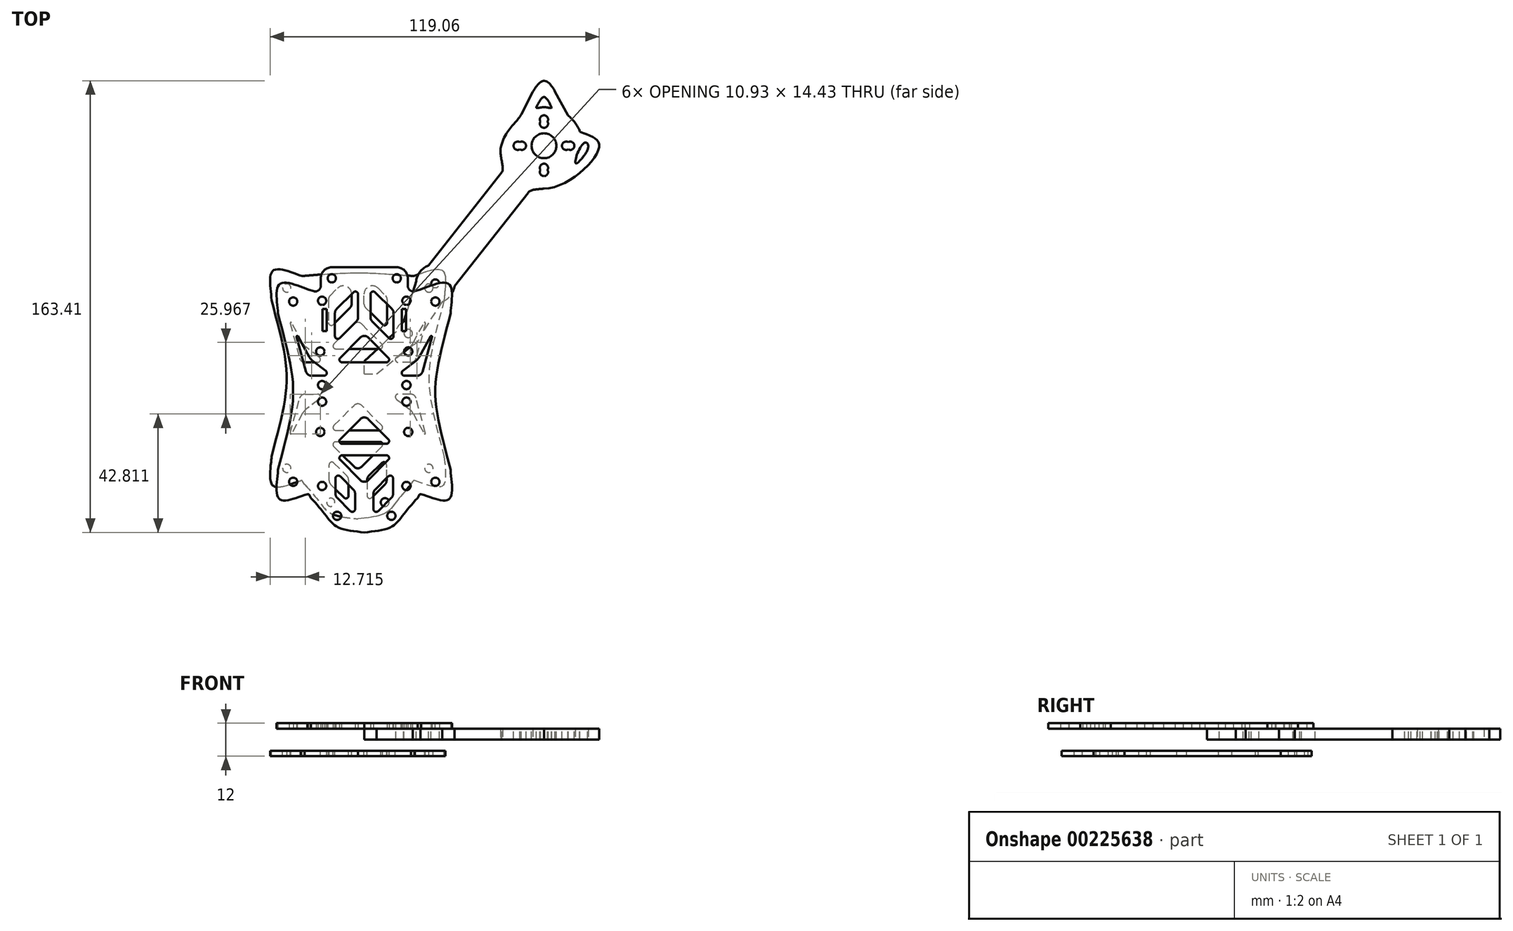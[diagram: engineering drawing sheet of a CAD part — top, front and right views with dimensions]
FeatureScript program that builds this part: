
annotation { "Feature Type Name" : "Feature", "Feature Type Description" : "" }
export const myFeature = defineFeature(function(context is Context, id is Id, definition is map)
    precondition{}
    {
        {
            var Q0;
            Q0=qCreatedBy(makeId("Top.planeOp"),FACE);
            var sketch = newSketch(context, id + "F0", { "sketchPlane" : qUnion([Q0])});
            skPoint(sketch, "E0.middle", {"position": v(0, -4.73) * mm});
            skLineSegment(sketch, "E1.bottom", {"start": v(25.7, 27.89) * mm, "end": v(-25.7, 27.89) * mm, "construction": true});
            skLineSegment(sketch, "E1.top", {"start": v(25.7, -37.35) * mm, "end": v(-25.7, -37.35) * mm, "construction": true});
            skLineSegment(sketch, "E1.left", {"start": v(25.7, 27.89) * mm, "end": v(25.7, -37.35) * mm, "construction": true});
            skLineSegment(sketch, "E1.right", {"start": v(-25.7, 27.89) * mm, "end": v(-25.7, -37.35) * mm, "construction": true});
            skLineSegment(sketch, "E2.bottom", {"start": v(-65, 77.77) * mm, "end": v(65, 77.77) * mm, "construction": true});
            skLineSegment(sketch, "E2.top", {"start": v(-65, -87.23) * mm, "end": v(65, -87.23) * mm, "construction": true});
            skLineSegment(sketch, "E2.left", {"start": v(-65, 77.77) * mm, "end": v(-65, -87.23) * mm, "construction": true});
            skLineSegment(sketch, "E2.right", {"start": v(65, 77.77) * mm, "end": v(65, -87.23) * mm, "construction": true});
            skCircle(sketch, "E3", {"center": v(65, 77.77) * mm, "radius": 4.5 * mm, "construction": true});
            skCircle(sketch, "E4", {"center": v(-65, 77.77) * mm, "radius": 4.5 * mm, "construction": true});
            skCircle(sketch, "E5", {"center": v(65, -87.23) * mm, "radius": 4.5 * mm, "construction": true});
            skCircle(sketch, "E6", {"center": v(-65, -87.23) * mm, "radius": 4.5 * mm, "construction": true});
            skCircle(sketch, "E7", {"center": v(65, 77.77) * mm, "radius": 8 * mm, "construction": true});
            skCircle(sketch, "E8", {"center": v(65, -87.23) * mm, "radius": 8 * mm, "construction": true});
            skCircle(sketch, "E9", {"center": v(-65, -87.23) * mm, "radius": 8 * mm, "construction": true});
            skCircle(sketch, "E10", {"center": v(-65, 77.77) * mm, "radius": 8 * mm, "construction": true});
            skCircle(sketch, "E11", {"center": v(65, 77.77) * mm, "radius": 9.5 * mm, "construction": true});
            skCircle(sketch, "E12", {"center": v(65, -87.23) * mm, "radius": 9.5 * mm, "construction": true});
            skCircle(sketch, "E13", {"center": v(-65, -87.23) * mm, "radius": 9.5 * mm, "construction": true});
            skCircle(sketch, "E14", {"center": v(-65, 77.77) * mm, "radius": 9.5 * mm, "construction": true});
            skCircle(sketch, "E15", {"center": v(65, 77.77) * mm, "radius": 14 * mm, "construction": true});
            skCircle(sketch, "E16", {"center": v(-65, 77.77) * mm, "radius": 14 * mm, "construction": true});
            skCircle(sketch, "E17", {"center": v(65, -87.23) * mm, "radius": 14 * mm, "construction": true});
            skCircle(sketch, "E18", {"center": v(-65, -87.23) * mm, "radius": 14 * mm, "construction": true});
            skCircle(sketch, "E19", {"center": v(65, 77.77) * mm, "radius": 63.5 * mm, "construction": true});
            skCircle(sketch, "E20", {"center": v(65, -87.23) * mm, "radius": 63.5 * mm, "construction": true});
            skCircle(sketch, "E21", {"center": v(-65, -87.23) * mm, "radius": 63.5 * mm, "construction": true});
            skCircle(sketch, "E22", {"center": v(-65, 77.77) * mm, "radius": 63.5 * mm, "construction": true});
            skLineSegment(sketch, "E23.bottom", {"start": v(-26.2, 21.46) * mm, "end": v(26.2, 21.46) * mm, "construction": true});
            skLineSegment(sketch, "E23.top", {"start": v(-26.19, -30.92) * mm, "end": v(26.2, -30.92) * mm, "construction": true});
            skLineSegment(sketch, "E23.left", {"start": v(-26.2, 21.46) * mm, "end": v(-26.2, -30.92) * mm, "construction": true});
            skLineSegment(sketch, "E23.right", {"start": v(26.2, 21.46) * mm, "end": v(26.2, -30.92) * mm, "construction": true});
            skCircle(sketch, "E24", {"center": v(25.7, 27.89) * mm, "radius": 1.5 * mm, "construction": true});
            skCircle(sketch, "E25", {"center": v(-25.7, 27.89) * mm, "radius": 1.5 * mm, "construction": true});
            skCircle(sketch, "E26", {"center": v(25.7, -37.35) * mm, "radius": 1.5 * mm, "construction": true});
            skCircle(sketch, "E27", {"center": v(-25.7, -37.35) * mm, "radius": 1.5 * mm, "construction": true});
            skLineSegment(sketch, "E28", {"start": v(-65, 77.77) * mm, "end": v(65, -87.23) * mm, "construction": true});
            skLineSegment(sketch, "E29", {"start": v(65, 77.77) * mm, "end": v(-65, -87.23) * mm, "construction": true});
            skLineSegment(sketch, "E30.bottom", {"start": v(-15.25, -8.35) * mm, "end": v(15.25, -8.35) * mm, "construction": true});
            skLineSegment(sketch, "E30.top", {"start": v(-15.25, -38.85) * mm, "end": v(15.25, -38.85) * mm, "construction": true});
            skLineSegment(sketch, "E30.left", {"start": v(-15.25, -8.35) * mm, "end": v(-15.25, -38.85) * mm, "construction": true});
            skLineSegment(sketch, "E30.right", {"start": v(15.25, -8.35) * mm, "end": v(15.25, -38.85) * mm, "construction": true});
            skPoint(sketch, "E30.middle", {"position": v(0, -23.6) * mm});
            skLineSegment(sketch, "E31.bottom", {"start": v(-15.25, 28.15) * mm, "end": v(15.25, 28.15) * mm, "construction": true});
            skLineSegment(sketch, "E31.top", {"start": v(-15.25, -2.35) * mm, "end": v(15.25, -2.35) * mm, "construction": true});
            skLineSegment(sketch, "E31.left", {"start": v(-15.25, 28.15) * mm, "end": v(-15.25, -2.35) * mm, "construction": true});
            skLineSegment(sketch, "E31.right", {"start": v(15.25, 28.15) * mm, "end": v(15.25, -2.35) * mm, "construction": true});
            skPoint(sketch, "E31.middle", {"position": v(0, 12.9) * mm});
            skLineSegment(sketch, "E32", {"start": v(0, -2.35) * mm, "end": v(0, -8.35) * mm, "construction": true});
            skLineSegment(sketch, "E33", {"start": v(0, 36.28) * mm, "end": v(-11.75, 36.28) * mm, "construction": true});
            skLineSegment(sketch, "E34", {"start": v(0, 36.28) * mm, "end": v(11.75, 36.28) * mm, "construction": true});
            skLineSegment(sketch, "E35", {"start": v(-25.7, 27.89) * mm, "end": v(-20.2, 32.22) * mm, "construction": true});
            skLineSegment(sketch, "E36", {"start": v(-25.7, 27.89) * mm, "end": v(-31.2, 23.56) * mm, "construction": true});
            skLineSegment(sketch, "E37", {"start": v(-25.7, 27.89) * mm, "end": v(-30.65, 34.17) * mm, "construction": true});
            skLineSegment(sketch, "E38", {"start": v(25.7, 27.89) * mm, "end": v(30.65, 34.17) * mm, "construction": true});
            skLineSegment(sketch, "E39", {"start": v(25.7, 27.89) * mm, "end": v(20.2, 32.22) * mm, "construction": true});
            skLineSegment(sketch, "E40", {"start": v(25.7, 27.89) * mm, "end": v(31.2, 23.56) * mm, "construction": true});
            skLineSegment(sketch, "E41", {"start": v(25.7, -37.35) * mm, "end": v(30.65, -43.64) * mm, "construction": true});
            skLineSegment(sketch, "E42", {"start": v(25.7, -37.35) * mm, "end": v(20.2, -41.68) * mm, "construction": true});
            skLineSegment(sketch, "E43", {"start": v(25.7, -37.35) * mm, "end": v(31.2, -33.02) * mm, "construction": true});
            skLineSegment(sketch, "E44", {"start": v(-25.7, -37.35) * mm, "end": v(-30.65, -43.64) * mm, "construction": true});
            skLineSegment(sketch, "E45", {"start": v(-25.7, -37.35) * mm, "end": v(-20.2, -41.68) * mm, "construction": true});
            skLineSegment(sketch, "E46", {"start": v(-25.7, -37.35) * mm, "end": v(-31.2, -33.02) * mm, "construction": true});
            skFitSpline(sketch, "E47", {"points": [v(-20.2, 32.22) * mm, v(-30.65, 34.17) * mm, v(-31.2, 23.56) * mm], "startDerivative": vector(-20.3, 7.46) * mm, "endDerivative": vector(0.93, -21.61) * mm});
            skFitSpline(sketch, "E48", {"points": [v(20.2, 32.22) * mm, v(30.65, 34.17) * mm, v(31.2, 23.56) * mm], "startDerivative": vector(20.3, 7.46) * mm, "endDerivative": vector(-0.93, -21.61) * mm});
            skLineSegment(sketch, "E49", {"start": v(-11.75, 36.28) * mm, "end": v(-15.75, 36.28) * mm, "construction": true});
            skLineSegment(sketch, "E50", {"start": v(11.75, 36.28) * mm, "end": v(15.75, 36.28) * mm, "construction": true});
            skCircle(sketch, "E51", {"center": v(-11.75, 36.28) * mm, "radius": 1.5 * mm});
            skCircle(sketch, "E52", {"center": v(11.75, 36.28) * mm, "radius": 1.5 * mm});
            skLineSegment(sketch, "E53", {"start": v(0, 36.28) * mm, "end": v(0, 40.28) * mm, "construction": true});
            skLineSegment(sketch, "E54", {"start": v(-15.75, 36.28) * mm, "end": v(-15.75, 36.28) * mm});
            skLineSegment(sketch, "E55", {"start": v(-11.75, 40.28) * mm, "end": v(0, 40.28) * mm});
            skLineSegment(sketch, "E56", {"start": v(0, 40.28) * mm, "end": v(11.75, 40.28) * mm});
            skLineSegment(sketch, "E57", {"start": v(15.75, 36.28) * mm, "end": v(15.75, 36.28) * mm});
            skPoint(sketch, "E58.visualSharp", {"position": v(-15.75, 40.28) * mm});
            skArc(sketch, "E58.filletArc", {"start": v(-11.75, 40.28) * mm, "mid": v(-14.58, 39.1) * mm, "end": v(-15.75, 36.28) * mm});
            skPoint(sketch, "E59.visualSharp", {"position": v(15.75, 40.28) * mm});
            skArc(sketch, "E59.filletArc", {"start": v(15.75, 36.28) * mm, "mid": v(14.58, 39.1) * mm, "end": v(11.75, 40.28) * mm});
            skLineSegment(sketch, "E60", {"start": v(-20.2, 32.22) * mm, "end": v(-18.34, 31.65) * mm});
            skLineSegment(sketch, "E61", {"start": v(-15.75, 33.56) * mm, "end": v(-15.75, 36.28) * mm});
            skPoint(sketch, "E62.visualSharp", {"position": v(-15.75, 30.85) * mm});
            skArc(sketch, "E62.filletArc", {"start": v(-18.34, 31.65) * mm, "mid": v(-16.56, 31.95) * mm, "end": v(-15.75, 33.56) * mm});
            skLineSegment(sketch, "E63", {"start": v(-15.75, 30.85) * mm, "end": v(0, 30.85) * mm, "construction": true});
            skLineSegment(sketch, "E64", {"start": v(0, 30.85) * mm, "end": v(15.75, 30.85) * mm, "construction": true});
            skLineSegment(sketch, "E65", {"start": v(20.2, 32.22) * mm, "end": v(18.34, 31.65) * mm});
            skLineSegment(sketch, "E66", {"start": v(15.75, 36.28) * mm, "end": v(15.75, 33.56) * mm});
            skPoint(sketch, "E67.visualSharp", {"position": v(15.75, 30.85) * mm});
            skArc(sketch, "E67.filletArc", {"start": v(15.75, 33.56) * mm, "mid": v(16.56, 31.95) * mm, "end": v(18.34, 31.65) * mm});
            skCircle(sketch, "E68", {"center": v(-15.25, -38.85) * mm, "radius": 1.5 * mm});
            skCircle(sketch, "E69", {"center": v(15.25, -38.85) * mm, "radius": 1.5 * mm});
            skLineSegment(sketch, "E70", {"start": v(0, -38.85) * mm, "end": v(0, -42.85) * mm, "construction": true});
            skLineSegment(sketch, "E71", {"start": v(-15.25, -38.85) * mm, "end": v(-19.25, -38.85) * mm, "construction": true});
            skLineSegment(sketch, "E72", {"start": v(15.25, -38.85) * mm, "end": v(19.25, -38.85) * mm, "construction": true});
            skLineSegment(sketch, "E73", {"start": v(-19.25, -43.2) * mm, "end": v(0, -43.2) * mm, "construction": true});
            skLineSegment(sketch, "E74", {"start": v(0, -43.2) * mm, "end": v(19.25, -43.2) * mm, "construction": true});
            skPoint(sketch, "E75.visualSharp", {"position": v(-19.25, -43.2) * mm});
            skPoint(sketch, "E76.visualSharp", {"position": v(19.25, -43.2) * mm});
            skCircle(sketch, "E77", {"center": v(-9.8, -49.64) * mm, "radius": 1.5 * mm});
            skCircle(sketch, "E78", {"center": v(9.8, -49.64) * mm, "radius": 1.5 * mm});
            skLineSegment(sketch, "E79", {"start": v(-9.8, -49.64) * mm, "end": v(0, -49.64) * mm, "construction": true});
            skLineSegment(sketch, "E80", {"start": v(0, -49.64) * mm, "end": v(9.8, -49.64) * mm, "construction": true});
            skFitSpline(sketch, "E81", {"points": [v(-31.2, 23.56) * mm, v(-25.7, -4.73) * mm, v(-31.2, -33.02) * mm], "startDerivative": vector(16.96, -67.18) * mm, "endDerivative": vector(-16.96, -67.18) * mm});
            skFitSpline(sketch, "E82", {"points": [v(31.2, 23.56) * mm, v(25.7, -4.73) * mm, v(31.2, -33.02) * mm], "startDerivative": vector(-16.96, -67.18) * mm, "endDerivative": vector(16.96, -67.18) * mm});
            skLineSegment(sketch, "E83", {"start": v(0, -49.64) * mm, "end": v(0, -55.64) * mm, "construction": true});
            skLineSegment(sketch, "E84", {"start": v(-9.8, -49.64) * mm, "end": v(-13.8, -49.64) * mm, "construction": true});
            skLineSegment(sketch, "E85", {"start": v(-9.8, -49.64) * mm, "end": v(-9.8, -53.64) * mm, "construction": true});
            skLineSegment(sketch, "E86", {"start": v(9.8, -49.64) * mm, "end": v(13.8, -49.64) * mm, "construction": true});
            skLineSegment(sketch, "E87", {"start": v(9.8, -49.64) * mm, "end": v(9.8, -53.64) * mm, "construction": true});
            skCircle(sketch, "E88", {"center": v(-25.7, 27.89) * mm, "radius": 1.5 * mm});
            skCircle(sketch, "E89", {"center": v(25.7, 27.89) * mm, "radius": 1.5 * mm});
            skCircle(sketch, "E90", {"center": v(-25.7, -37.35) * mm, "radius": 1.5 * mm});
            skCircle(sketch, "E91", {"center": v(25.7, -37.35) * mm, "radius": 1.5 * mm});
            skLineSegment(sketch, "E92", {"start": v(0, 27.89) * mm, "end": v(0, 36.28) * mm, "construction": true});
            skLineSegment(sketch, "E93", {"start": v(117.55, -29.37) * mm, "end": v(117.55, 4.6) * mm, "construction": true});
            skLineSegment(sketch, "E94", {"start": v(-19.04, -41.25) * mm, "end": v(0, -41.25) * mm, "construction": true});
            skLineSegment(sketch, "E95", {"start": v(0, -41.25) * mm, "end": v(19.04, -41.25) * mm, "construction": true});
            skFitSpline(sketch, "E96", {"points": [v(-19.25, -43.2) * mm, v(-13.8, -49.64) * mm, v(-9.8, -53.64) * mm, v(0, -55.64) * mm], "startDerivative": vector(17.01, -18.5) * mm, "endDerivative": vector(29.8, -3.11) * mm});
            skFitSpline(sketch, "E97", {"points": [v(19.25, -43.2) * mm, v(13.8, -49.64) * mm, v(9.8, -53.64) * mm, v(0, -55.64) * mm], "startDerivative": vector(-17.98, -19.6) * mm, "endDerivative": vector(-29.8, -3.11) * mm});
            skLineSegment(sketch, "E98", {"start": v(118.58, 5.6) * mm, "end": v(171.8, 3.95) * mm, "construction": true});
            skPoint(sketch, "E99.visualSharp", {"position": v(117.55, 5.63) * mm});
            skArc(sketch, "E99.filletArc", {"start": v(118.58, 5.6) * mm, "mid": v(117.85, 5.32) * mm, "end": v(117.55, 4.6) * mm, "construction": true});
            skPoint(sketch, "E100.visualSharp", {"position": v(19.04, -41.25) * mm});
            skPoint(sketch, "E101.visualSharp", {"position": v(-19.04, -41.25) * mm});
            skLineSegment(sketch, "E102.bottom", {"start": v(-13.78, 12.77) * mm, "end": v(13.78, 12.77) * mm, "construction": true});
            skLineSegment(sketch, "E102.top", {"start": v(-13.78, -22.23) * mm, "end": v(13.78, -22.23) * mm, "construction": true});
            skLineSegment(sketch, "E102.left", {"start": v(-13.78, 12.77) * mm, "end": v(-13.78, -22.23) * mm, "construction": true});
            skLineSegment(sketch, "E102.right", {"start": v(13.78, 12.77) * mm, "end": v(13.78, -22.23) * mm, "construction": true});
            skCircle(sketch, "E103", {"center": v(-15.25, -8.35) * mm, "radius": 1.5 * mm});
            skCircle(sketch, "E104", {"center": v(15.25, -8.35) * mm, "radius": 1.5 * mm});
            skCircle(sketch, "E105", {"center": v(15.25, -2.35) * mm, "radius": 1.5 * mm});
            skCircle(sketch, "E106", {"center": v(-15.25, -2.35) * mm, "radius": 1.5 * mm});
            skCircle(sketch, "E107", {"center": v(-15.25, 28.15) * mm, "radius": 1.5 * mm});
            skCircle(sketch, "E108", {"center": v(15.25, 28.15) * mm, "radius": 1.5 * mm});
            skLineSegment(sketch, "E109", {"start": v(0, 8.34) * mm, "end": v(-18.2, 8.34) * mm, "construction": true});
            skLineSegment(sketch, "E110", {"start": v(0, 8.34) * mm, "end": v(18.2, 8.34) * mm, "construction": true});
            skLineSegment(sketch, "E111", {"start": v(0, -4.73) * mm, "end": v(0, 9.53) * mm, "construction": true});
            skLineSegment(sketch, "E112", {"start": v(0, -4.73) * mm, "end": v(17, -4.73) * mm, "construction": true});
            skLineSegment(sketch, "E113.bottom", {"start": v(-15.9, 9.82) * mm, "end": v(15.9, 9.82) * mm, "construction": true});
            skLineSegment(sketch, "E113.top", {"start": v(-15.9, -19.29) * mm, "end": v(15.9, -19.29) * mm, "construction": true});
            skLineSegment(sketch, "E113.left", {"start": v(-15.9, 9.82) * mm, "end": v(-15.9, -19.29) * mm, "construction": true});
            skLineSegment(sketch, "E113.right", {"start": v(15.9, 9.82) * mm, "end": v(15.9, -19.29) * mm, "construction": true});
            skCircle(sketch, "E114", {"center": v(15.9, 9.82) * mm, "radius": 1.5 * mm});
            skCircle(sketch, "E115", {"center": v(15.9, -19.29) * mm, "radius": 1.5 * mm});
            skCircle(sketch, "E116", {"center": v(-15.9, -19.29) * mm, "radius": 1.5 * mm});
            skCircle(sketch, "E117", {"center": v(-15.9, 9.82) * mm, "radius": 1.5 * mm});
            skLineSegment(sketch, "E118", {"start": v(0, 21.19) * mm, "end": v(14.33, 21.19) * mm, "construction": true});
            skLineSegment(sketch, "E119", {"start": v(0, 21.19) * mm, "end": v(-14.33, 21.19) * mm, "construction": true});
            skLineSegment(sketch, "E120.bottom", {"start": v(-15.08, 25.19) * mm, "end": v(-13.58, 25.19) * mm});
            skLineSegment(sketch, "E120.top", {"start": v(-15.08, 17.19) * mm, "end": v(-13.58, 17.19) * mm});
            skLineSegment(sketch, "E120.left", {"start": v(-15.08, 25.19) * mm, "end": v(-15.08, 17.19) * mm});
            skLineSegment(sketch, "E120.right", {"start": v(-13.58, 25.19) * mm, "end": v(-13.58, 17.19) * mm});
            skPoint(sketch, "E120.middle", {"position": v(-14.33, 21.19) * mm});
            skLineSegment(sketch, "E121.bottom", {"start": v(15.08, 25.19) * mm, "end": v(13.58, 25.19) * mm});
            skLineSegment(sketch, "E121.top", {"start": v(15.08, 17.19) * mm, "end": v(13.58, 17.19) * mm});
            skLineSegment(sketch, "E121.left", {"start": v(15.08, 25.19) * mm, "end": v(15.08, 17.19) * mm});
            skLineSegment(sketch, "E121.right", {"start": v(13.58, 25.19) * mm, "end": v(13.58, 17.19) * mm});
            skPoint(sketch, "E121.middle", {"position": v(14.33, 21.19) * mm});
            skFitSpline(sketch, "E122", {"points": [v(-31.2, -33.02) * mm, v(-30.65, -43.64) * mm, v(-20.6, -41.83) * mm], "startDerivative": vector(-1.92, -24.87) * mm, "endDerivative": vector(23.17, 7.34) * mm});
            skLineSegment(sketch, "E123", {"start": v(-20.6, -41.83) * mm, "end": v(0, -41.83) * mm, "construction": true});
            skLineSegment(sketch, "E124", {"start": v(0, -41.83) * mm, "end": v(20.6, -41.83) * mm, "construction": true});
            skLineSegment(sketch, "E125", {"start": v(19.25, -43.2) * mm, "end": v(19.99, -42.02) * mm});
            skLineSegment(sketch, "E126", {"start": v(20.58, -41.82) * mm, "end": v(20.6, -41.83) * mm});
            skLineSegment(sketch, "E127", {"start": v(-19.25, -43.2) * mm, "end": v(-19.99, -42.02) * mm});
            skLineSegment(sketch, "E128", {"start": v(-20.58, -41.82) * mm, "end": v(-20.6, -41.83) * mm});
            skLineSegment(sketch, "E129", {"start": v(171.8, 3.95) * mm, "end": v(171.8, -18.5) * mm, "construction": true});
            skPoint(sketch, "E130.visualSharp", {"position": v(20.2, -41.68) * mm});
            skArc(sketch, "E130.filletArc", {"start": v(20.58, -41.82) * mm, "mid": v(20.25, -41.82) * mm, "end": v(19.99, -42.02) * mm});
            skPoint(sketch, "E131.visualSharp", {"position": v(-20.2, -41.68) * mm});
            skArc(sketch, "E131.filletArc", {"start": v(-19.99, -42.02) * mm, "mid": v(-20.25, -41.82) * mm, "end": v(-20.58, -41.82) * mm});
            skLineSegment(sketch, "E132", {"start": v(0, -4.73) * mm, "end": v(0, -1.43) * mm, "construction": true});
            skLineSegment(sketch, "E133.bottom", {"start": v(-5.5, 0.77) * mm, "end": v(5.5, 0.77) * mm, "construction": true});
            skLineSegment(sketch, "E133.top", {"start": v(-5.5, -10.23) * mm, "end": v(5.5, -10.23) * mm, "construction": true});
            skLineSegment(sketch, "E133.left", {"start": v(-5.5, 0.77) * mm, "end": v(-5.5, -10.23) * mm, "construction": true});
            skLineSegment(sketch, "E133.right", {"start": v(5.5, 0.77) * mm, "end": v(5.5, -10.23) * mm, "construction": true});
            skLineSegment(sketch, "E134.bottom", {"start": v(-7.98, 5.89) * mm, "end": v(7.98, 5.89) * mm});
            skPoint(sketch, "E134.middle", {"position": v(0, 7.86) * mm});
            skPoint(sketch, "E135.middle", {"position": v(0, -31.33) * mm});
            skPoint(sketch, "E136", {"position": v(0, -22.23) * mm});
            skPoint(sketch, "E137", {"position": v(0, -30.92) * mm});
            skLineSegment(sketch, "E138", {"start": v(-8.69, 7.6) * mm, "end": v(-1.41, 14.87) * mm});
            skLineSegment(sketch, "E139", {"start": v(1.41, 14.87) * mm, "end": v(8.69, 7.6) * mm});
            skPoint(sketch, "E140.visualSharp", {"position": v(0, 16.28) * mm});
            skArc(sketch, "E140.filletArc", {"start": v(1.41, 14.87) * mm, "mid": v(0, 15.46) * mm, "end": v(-1.41, 14.87) * mm});
            skPoint(sketch, "E141.visualSharp", {"position": v(-10.4, 5.89) * mm});
            skArc(sketch, "E141.filletArc", {"start": v(-8.69, 7.6) * mm, "mid": v(-8.9, 6.5) * mm, "end": v(-7.98, 5.89) * mm});
            skPoint(sketch, "E142.visualSharp", {"position": v(10.4, 5.89) * mm});
            skArc(sketch, "E142.filletArc", {"start": v(7.98, 5.89) * mm, "mid": v(8.9, 6.5) * mm, "end": v(8.69, 7.6) * mm});
            skPoint(sketch, "E143.visualSharp", {"position": v(0, -4.14) * mm});
            skLineSegment(sketch, "E144", {"start": v(1, 5.89) * mm, "end": v(1, 1.39) * mm, "construction": true});
            skPoint(sketch, "E145.middle", {"position": v(0, 4.86) * mm});
            skCircle(sketch, "E146", {"center": v(15.9, 9.82) * mm, "radius": 4.5 * mm, "construction": true});
            skCircle(sketch, "E147", {"center": v(-15.9, 9.82) * mm, "radius": 4.5 * mm, "construction": true});
            skCircle(sketch, "E148", {"center": v(15.9, -19.29) * mm, "radius": 4.5 * mm, "construction": true});
            skCircle(sketch, "E149", {"center": v(-15.9, -19.29) * mm, "radius": 4.5 * mm, "construction": true});
            skLineSegment(sketch, "E150", {"start": v(0, -4.73) * mm, "end": v(-15.9, 9.82) * mm, "construction": true});
            skLineSegment(sketch, "E151", {"start": v(0, -4.73) * mm, "end": v(15.9, 9.82) * mm, "construction": true});
            skLineSegment(sketch, "E152", {"start": v(15.9, 9.82) * mm, "end": v(25.7, 27.89) * mm, "construction": true});
            skLineSegment(sketch, "E153", {"start": v(-15.9, 9.82) * mm, "end": v(-25.7, 27.89) * mm, "construction": true});
            skLineSegment(sketch, "E154", {"start": v(0, -4.73) * mm, "end": v(-15.9, -19.29) * mm, "construction": true});
            skLineSegment(sketch, "E155", {"start": v(-15.9, -19.29) * mm, "end": v(-25.7, -37.35) * mm, "construction": true});
            skLineSegment(sketch, "E156", {"start": v(0, -4.73) * mm, "end": v(15.9, -19.29) * mm, "construction": true});
            skLineSegment(sketch, "E157", {"start": v(15.9, -19.29) * mm, "end": v(25.7, -37.35) * mm, "construction": true});
            skLineSegment(sketch, "E158", {"start": v(-2.25, 22.16) * mm, "end": v(-2.25, 30.51) * mm});
            skLineSegment(sketch, "E159", {"start": v(2.25, 22.16) * mm, "end": v(2.25, 30.51) * mm});
            skLineSegment(sketch, "E160", {"start": v(-3.95, 31.22) * mm, "end": v(-10.02, 25.16) * mm});
            skLineSegment(sketch, "E161", {"start": v(-10.6, 23.74) * mm, "end": v(-10.6, 15.38) * mm});
            skLineSegment(sketch, "E162", {"start": v(3.95, 31.22) * mm, "end": v(10.02, 25.16) * mm});
            skLineSegment(sketch, "E163", {"start": v(10.6, 23.74) * mm, "end": v(10.6, 15.38) * mm});
            skLineSegment(sketch, "E164", {"start": v(-8.9, 14.68) * mm, "end": v(-2.83, 20.74) * mm});
            skLineSegment(sketch, "E165", {"start": v(2.83, 20.74) * mm, "end": v(8.9, 14.68) * mm});
            skPoint(sketch, "E166.visualSharp", {"position": v(-2.25, 32.93) * mm});
            skArc(sketch, "E166.filletArc", {"start": v(-2.25, 30.51) * mm, "mid": v(-2.86, 31.44) * mm, "end": v(-3.95, 31.22) * mm});
            skPoint(sketch, "E167.visualSharp", {"position": v(-10.6, 24.57) * mm});
            skArc(sketch, "E167.filletArc", {"start": v(-10.02, 25.16) * mm, "mid": v(-10.45, 24.5) * mm, "end": v(-10.6, 23.74) * mm});
            skPoint(sketch, "E168.visualSharp", {"position": v(-2.25, 21.33) * mm});
            skArc(sketch, "E168.filletArc", {"start": v(-2.83, 20.74) * mm, "mid": v(-2.4, 21.4) * mm, "end": v(-2.25, 22.16) * mm});
            skPoint(sketch, "E169.visualSharp", {"position": v(2.25, 21.33) * mm});
            skArc(sketch, "E169.filletArc", {"start": v(2.25, 22.16) * mm, "mid": v(2.4, 21.4) * mm, "end": v(2.83, 20.74) * mm});
            skPoint(sketch, "E170.visualSharp", {"position": v(10.6, 24.57) * mm});
            skArc(sketch, "E170.filletArc", {"start": v(10.6, 23.74) * mm, "mid": v(10.45, 24.5) * mm, "end": v(10.02, 25.16) * mm});
            skPoint(sketch, "E171.visualSharp", {"position": v(2.25, 32.93) * mm});
            skArc(sketch, "E171.filletArc", {"start": v(3.95, 31.22) * mm, "mid": v(2.86, 31.44) * mm, "end": v(2.25, 30.51) * mm});
            skPoint(sketch, "E172.visualSharp", {"position": v(10.6, 12.97) * mm});
            skArc(sketch, "E172.filletArc", {"start": v(8.9, 14.68) * mm, "mid": v(9.99, 14.46) * mm, "end": v(10.6, 15.38) * mm});
            skPoint(sketch, "E173.visualSharp", {"position": v(-10.6, 12.97) * mm});
            skArc(sketch, "E173.filletArc", {"start": v(-10.6, 15.38) * mm, "mid": v(-9.99, 14.46) * mm, "end": v(-8.9, 14.68) * mm});
            skLineSegment(sketch, "E174", {"start": v(0, -27.75) * mm, "end": v(-7.99, -27.75) * mm});
            skLineSegment(sketch, "E175", {"start": v(0, -27.75) * mm, "end": v(7.99, -27.75) * mm});
            skLineSegment(sketch, "E176", {"start": v(-8.7, -29.46) * mm, "end": v(-1.41, -36.74) * mm});
            skLineSegment(sketch, "E177", {"start": v(8.7, -29.46) * mm, "end": v(1.41, -36.74) * mm});
            skPoint(sketch, "E178.visualSharp", {"position": v(10.4, -27.75) * mm});
            skArc(sketch, "E178.filletArc", {"start": v(8.7, -29.46) * mm, "mid": v(8.9, -28.37) * mm, "end": v(7.99, -27.75) * mm});
            skPoint(sketch, "E179.visualSharp", {"position": v(-10.4, -27.75) * mm});
            skArc(sketch, "E179.filletArc", {"start": v(-7.99, -27.75) * mm, "mid": v(-8.9, -28.37) * mm, "end": v(-8.7, -29.46) * mm});
            skPoint(sketch, "E180.visualSharp", {"position": v(0, -38.15) * mm});
            skArc(sketch, "E180.filletArc", {"start": v(-1.41, -36.74) * mm, "mid": v(0, -37.32) * mm, "end": v(1.41, -36.74) * mm});
            skFitSpline(sketch, "E181", {"points": [v(31.2, -33.02) * mm, v(30.65, -43.64) * mm, v(20.6, -41.83) * mm], "startDerivative": vector(1.93, -24.89) * mm, "endDerivative": vector(-23.2, 7.39) * mm});
            skLineSegment(sketch, "E182", {"start": v(-8.7, -35.4) * mm, "end": v(-3.91, -40.17) * mm});
            skLineSegment(sketch, "E183", {"start": v(8.7, -35.4) * mm, "end": v(3.91, -40.17) * mm});
            skLineSegment(sketch, "E184", {"start": v(-3.33, -41.59) * mm, "end": v(-3.33, -47.23) * mm});
            skLineSegment(sketch, "E185", {"start": v(-5.04, -47.93) * mm, "end": v(-9.81, -43.15) * mm});
            skLineSegment(sketch, "E186", {"start": v(-10.4, -41.74) * mm, "end": v(-10.4, -36.1) * mm});
            skLineSegment(sketch, "E187", {"start": v(3.33, -41.59) * mm, "end": v(3.33, -47.23) * mm});
            skLineSegment(sketch, "E188", {"start": v(5.04, -47.93) * mm, "end": v(9.81, -43.15) * mm});
            skLineSegment(sketch, "E189", {"start": v(10.4, -41.74) * mm, "end": v(10.4, -36.1) * mm});
            skPoint(sketch, "E190.visualSharp", {"position": v(10.4, -33.69) * mm});
            skArc(sketch, "E190.filletArc", {"start": v(10.4, -36.1) * mm, "mid": v(9.78, -35.18) * mm, "end": v(8.7, -35.4) * mm});
            skPoint(sketch, "E191.visualSharp", {"position": v(3.33, -49.64) * mm});
            skArc(sketch, "E191.filletArc", {"start": v(3.33, -47.23) * mm, "mid": v(3.95, -48.15) * mm, "end": v(5.04, -47.93) * mm});
            skPoint(sketch, "E192.visualSharp", {"position": v(-3.33, -49.64) * mm});
            skArc(sketch, "E192.filletArc", {"start": v(-5.04, -47.93) * mm, "mid": v(-3.95, -48.15) * mm, "end": v(-3.33, -47.23) * mm});
            skPoint(sketch, "E193.visualSharp", {"position": v(-10.4, -33.69) * mm});
            skArc(sketch, "E193.filletArc", {"start": v(-8.7, -35.4) * mm, "mid": v(-9.78, -35.18) * mm, "end": v(-10.4, -36.1) * mm});
            skPoint(sketch, "E194.visualSharp", {"position": v(-3.33, -40.76) * mm});
            skArc(sketch, "E194.filletArc", {"start": v(-3.33, -41.59) * mm, "mid": v(-3.48, -40.82) * mm, "end": v(-3.91, -40.17) * mm});
            skPoint(sketch, "E195.visualSharp", {"position": v(-10.4, -42.57) * mm});
            skArc(sketch, "E195.filletArc", {"start": v(-10.4, -41.74) * mm, "mid": v(-10.25, -42.5) * mm, "end": v(-9.81, -43.15) * mm});
            skPoint(sketch, "E196.visualSharp", {"position": v(3.33, -40.76) * mm});
            skArc(sketch, "E196.filletArc", {"start": v(3.91, -40.17) * mm, "mid": v(3.48, -40.82) * mm, "end": v(3.33, -41.59) * mm});
            skPoint(sketch, "E197.visualSharp", {"position": v(10.4, -42.57) * mm});
            skArc(sketch, "E197.filletArc", {"start": v(9.81, -43.15) * mm, "mid": v(10.25, -42.5) * mm, "end": v(10.4, -41.74) * mm});
            skLineSegment(sketch, "E198", {"start": v(0, -23.6) * mm, "end": v(-7.99, -23.6) * mm});
            skLineSegment(sketch, "E199", {"start": v(0, -23.6) * mm, "end": v(7.99, -23.6) * mm});
            skLineSegment(sketch, "E200", {"start": v(-8.7, -21.89) * mm, "end": v(-1.41, -14.61) * mm});
            skLineSegment(sketch, "E201", {"start": v(8.7, -21.89) * mm, "end": v(1.41, -14.61) * mm});
            skPoint(sketch, "E202.visualSharp", {"position": v(0, -13.2) * mm});
            skArc(sketch, "E202.filletArc", {"start": v(1.41, -14.61) * mm, "mid": v(0, -14.02) * mm, "end": v(-1.41, -14.61) * mm});
            skPoint(sketch, "E203.visualSharp", {"position": v(-10.4, -23.6) * mm});
            skArc(sketch, "E203.filletArc", {"start": v(-8.7, -21.89) * mm, "mid": v(-8.9, -22.98) * mm, "end": v(-7.99, -23.6) * mm});
            skPoint(sketch, "E204.visualSharp", {"position": v(10.4, -23.6) * mm});
            skArc(sketch, "E204.filletArc", {"start": v(7.99, -23.6) * mm, "mid": v(8.9, -22.98) * mm, "end": v(8.7, -21.89) * mm});
            skLineSegment(sketch, "E205", {"start": v(17, -4.73) * mm, "end": v(20, -4.73) * mm, "construction": true});
            skCircle(sketch, "E206", {"center": v(25.7, 27.89) * mm, "radius": 7 * mm, "construction": true});
            skLineSegment(sketch, "E207", {"start": v(19.97, 8) * mm, "end": v(24.01, 15.34) * mm});
            skLineSegment(sketch, "E208", {"start": v(24.47, 15.15) * mm, "end": v(21.06, 2.52) * mm});
            skLineSegment(sketch, "E209", {"start": v(19.13, 1.04) * mm, "end": v(14.55, 1.04) * mm});
            skLineSegment(sketch, "E210", {"start": v(13.94, 2.83) * mm, "end": v(18.64, 6.44) * mm});
            skPoint(sketch, "E211.visualSharp", {"position": v(25.02, 17.15) * mm});
            skArc(sketch, "E211.filletArc", {"start": v(24.47, 15.15) * mm, "mid": v(24.33, 15.45) * mm, "end": v(24.01, 15.34) * mm});
            skPoint(sketch, "E212.visualSharp", {"position": v(20.66, 1.04) * mm});
            skArc(sketch, "E212.filletArc", {"start": v(19.13, 1.04) * mm, "mid": v(20.34, 1.45) * mm, "end": v(21.06, 2.52) * mm});
            skPoint(sketch, "E213.visualSharp", {"position": v(11.62, 1.04) * mm});
            skArc(sketch, "E213.filletArc", {"start": v(13.94, 2.83) * mm, "mid": v(13.6, 1.72) * mm, "end": v(14.55, 1.04) * mm});
            skPoint(sketch, "E214.visualSharp", {"position": v(19.46, 7.08) * mm});
            skArc(sketch, "E214.filletArc", {"start": v(18.64, 6.44) * mm, "mid": v(19.38, 7.15) * mm, "end": v(19.97, 8) * mm});
            skLineSegment(sketch, "E215", {"start": v(11.62, 1.04) * mm, "end": v(0, 1.04) * mm, "construction": true});
            skPoint(sketch, "E215.endSnap0", {"position": v(0, 0.77) * mm});
            skLineSegment(sketch, "E216", {"start": v(0, 1.04) * mm, "end": v(-11.62, 1.04) * mm, "construction": true});
            skLineSegment(sketch, "E217", {"start": v(-14.55, 1.04) * mm, "end": v(-19.13, 1.04) * mm});
            skLineSegment(sketch, "E218", {"start": v(19.46, 7.08) * mm, "end": v(0, 7.08) * mm, "construction": true});
            skLineSegment(sketch, "E219", {"start": v(0, 7.08) * mm, "end": v(-19.46, 7.08) * mm, "construction": true});
            skLineSegment(sketch, "E220", {"start": v(25.02, 17.15) * mm, "end": v(0, 17.15) * mm, "construction": true});
            skLineSegment(sketch, "E221", {"start": v(0, 17.15) * mm, "end": v(-25.02, 17.15) * mm, "construction": true});
            skLineSegment(sketch, "E222", {"start": v(-24.47, 15.15) * mm, "end": v(-21.06, 2.52) * mm});
            skLineSegment(sketch, "E223", {"start": v(-13.94, 2.83) * mm, "end": v(-18.64, 6.44) * mm});
            skLineSegment(sketch, "E224", {"start": v(-19.97, 8) * mm, "end": v(-24.01, 15.34) * mm});
            skPoint(sketch, "E225.visualSharp", {"position": v(-25.02, 17.15) * mm});
            skArc(sketch, "E225.filletArc", {"start": v(-24.01, 15.34) * mm, "mid": v(-24.33, 15.45) * mm, "end": v(-24.47, 15.15) * mm});
            skPoint(sketch, "E226.visualSharp", {"position": v(-11.62, 1.04) * mm});
            skArc(sketch, "E226.filletArc", {"start": v(-14.55, 1.04) * mm, "mid": v(-13.6, 1.72) * mm, "end": v(-13.94, 2.83) * mm});
            skPoint(sketch, "E227.visualSharp", {"position": v(-20.66, 1.04) * mm});
            skArc(sketch, "E227.filletArc", {"start": v(-21.06, 2.52) * mm, "mid": v(-20.34, 1.45) * mm, "end": v(-19.13, 1.04) * mm});
            skPoint(sketch, "E228.visualSharp", {"position": v(-19.46, 7.08) * mm});
            skArc(sketch, "E228.filletArc", {"start": v(-19.97, 8) * mm, "mid": v(-19.38, 7.15) * mm, "end": v(-18.64, 6.44) * mm});
            skSolve(sketch);
        }
        {
            var Q0;
            Q0=makeQuery(id+"F0.imprint","IMPRINT",FACE,{"disambiguationData":[TD([[makeQuery(id+"F0.imprint","IMPRINT",EDGE,{"derivedFrom":sQuery(id+"F0.wireOp",EDGE,"E47")}),1.0]])]});
            extrude(context, id + "F1", {"entities" : qUnion([Q0]), "depth" : 2 * mm});
        }
        {
            var Q0;
            Q0=qCreatedBy(makeId("Top.planeOp"),FACE);
            var sketch = newSketch(context, id + "F2", { "sketchPlane" : qUnion([Q0])});
            skPoint(sketch, "E229.middle", {"position": v(0, 1.77) * mm});
            skLineSegment(sketch, "E230.bottom", {"start": v(25.7, 34.4) * mm, "end": v(-25.7, 34.4) * mm, "construction": true});
            skLineSegment(sketch, "E230.top", {"start": v(25.7, -30.86) * mm, "end": v(-25.7, -30.86) * mm, "construction": true});
            skLineSegment(sketch, "E230.left", {"start": v(25.7, 34.4) * mm, "end": v(25.7, -30.86) * mm, "construction": true});
            skLineSegment(sketch, "E230.right", {"start": v(-25.7, 34.4) * mm, "end": v(-25.7, -30.86) * mm, "construction": true});
            skLineSegment(sketch, "E231.bottom", {"start": v(-65, 84.27) * mm, "end": v(65, 84.27) * mm, "construction": true});
            skLineSegment(sketch, "E231.top", {"start": v(-65, -80.73) * mm, "end": v(65, -80.73) * mm, "construction": true});
            skLineSegment(sketch, "E231.left", {"start": v(-65, 84.27) * mm, "end": v(-65, -80.73) * mm, "construction": true});
            skLineSegment(sketch, "E231.right", {"start": v(65, 84.27) * mm, "end": v(65, -80.73) * mm, "construction": true});
            skCircle(sketch, "E232", {"center": v(65, 84.27) * mm, "radius": 4.5 * mm, "construction": true});
            skCircle(sketch, "E233", {"center": v(-65, 84.27) * mm, "radius": 4.5 * mm, "construction": true});
            skCircle(sketch, "E234", {"center": v(65, -80.73) * mm, "radius": 4.5 * mm, "construction": true});
            skCircle(sketch, "E235", {"center": v(-65, -80.73) * mm, "radius": 4.5 * mm, "construction": true});
            skCircle(sketch, "E236", {"center": v(65, 84.27) * mm, "radius": 8 * mm, "construction": true});
            skCircle(sketch, "E237", {"center": v(65, -80.73) * mm, "radius": 8 * mm, "construction": true});
            skCircle(sketch, "E238", {"center": v(-65, -80.73) * mm, "radius": 8 * mm, "construction": true});
            skCircle(sketch, "E239", {"center": v(-65, 84.27) * mm, "radius": 8 * mm, "construction": true});
            skCircle(sketch, "E240", {"center": v(65, 84.27) * mm, "radius": 9.5 * mm, "construction": true});
            skCircle(sketch, "E241", {"center": v(65, -80.73) * mm, "radius": 9.5 * mm, "construction": true});
            skCircle(sketch, "E242", {"center": v(-65, -80.73) * mm, "radius": 9.5 * mm, "construction": true});
            skCircle(sketch, "E243", {"center": v(-65, 84.27) * mm, "radius": 9.5 * mm, "construction": true});
            skCircle(sketch, "E244", {"center": v(65, 84.27) * mm, "radius": 14 * mm, "construction": true});
            skCircle(sketch, "E245", {"center": v(-65, 84.27) * mm, "radius": 14 * mm, "construction": true});
            skCircle(sketch, "E246", {"center": v(65, -80.73) * mm, "radius": 14 * mm, "construction": true});
            skCircle(sketch, "E247", {"center": v(-65, -80.73) * mm, "radius": 14 * mm, "construction": true});
            skCircle(sketch, "E248", {"center": v(65, 84.27) * mm, "radius": 63.5 * mm, "construction": true});
            skCircle(sketch, "E249", {"center": v(65, -80.73) * mm, "radius": 63.5 * mm, "construction": true});
            skCircle(sketch, "E250", {"center": v(-65, -80.73) * mm, "radius": 63.5 * mm, "construction": true});
            skCircle(sketch, "E251", {"center": v(-65, 84.27) * mm, "radius": 63.5 * mm, "construction": true});
            skLineSegment(sketch, "E252.bottom", {"start": v(-26.2, 27.96) * mm, "end": v(26.19, 27.96) * mm, "construction": true});
            skLineSegment(sketch, "E252.top", {"start": v(-26.2, -24.42) * mm, "end": v(26.19, -24.42) * mm, "construction": true});
            skLineSegment(sketch, "E252.left", {"start": v(-26.2, 27.96) * mm, "end": v(-26.2, -24.42) * mm, "construction": true});
            skLineSegment(sketch, "E252.right", {"start": v(26.19, 27.96) * mm, "end": v(26.19, -24.42) * mm, "construction": true});
            skCircle(sketch, "E253", {"center": v(25.7, 34.4) * mm, "radius": 3.57 * mm, "construction": true});
            skCircle(sketch, "E254", {"center": v(-25.7, 34.4) * mm, "radius": 3.57 * mm, "construction": true});
            skCircle(sketch, "E255", {"center": v(25.7, -30.86) * mm, "radius": 3.57 * mm, "construction": true});
            skCircle(sketch, "E256", {"center": v(-25.7, -30.86) * mm, "radius": 3.57 * mm, "construction": true});
            skLineSegment(sketch, "E257", {"start": v(-65, 84.27) * mm, "end": v(65, -80.73) * mm, "construction": true});
            skLineSegment(sketch, "E258", {"start": v(65, 84.27) * mm, "end": v(-65, -80.73) * mm, "construction": true});
            skLineSegment(sketch, "E259.bottom", {"start": v(-15.25, -12) * mm, "end": v(15.25, -12) * mm, "construction": true});
            skLineSegment(sketch, "E259.top", {"start": v(-15.25, -42.5) * mm, "end": v(15.25, -42.5) * mm, "construction": true});
            skLineSegment(sketch, "E259.left", {"start": v(-15.25, -12) * mm, "end": v(-15.25, -42.5) * mm, "construction": true});
            skLineSegment(sketch, "E259.right", {"start": v(15.25, -12) * mm, "end": v(15.25, -42.5) * mm, "construction": true});
            skPoint(sketch, "E259.middle", {"position": v(0, -27.25) * mm});
            skLineSegment(sketch, "E260.bottom", {"start": v(-15.25, 29) * mm, "end": v(15.25, 29) * mm, "construction": true});
            skLineSegment(sketch, "E260.top", {"start": v(-15.25, -1.5) * mm, "end": v(15.25, -1.5) * mm, "construction": true});
            skLineSegment(sketch, "E260.left", {"start": v(-15.25, 29) * mm, "end": v(-15.25, -1.5) * mm, "construction": true});
            skPoint(sketch, "E260.middle", {"position": v(0, 13.75) * mm});
            skLineSegment(sketch, "E261", {"start": v(0, -1.5) * mm, "end": v(0, -12) * mm, "construction": true});
            skCircle(sketch, "E262", {"center": v(25.7, 34.4) * mm, "radius": 1.5 * mm, "construction": true});
            skCircle(sketch, "E263", {"center": v(-25.7, 34.4) * mm, "radius": 1.5 * mm, "construction": true});
            skCircle(sketch, "E264", {"center": v(25.7, -30.86) * mm, "radius": 1.5 * mm, "construction": true});
            skCircle(sketch, "E265", {"center": v(-25.7, -30.86) * mm, "radius": 1.5 * mm, "construction": true});
            skCircle(sketch, "E266", {"center": v(25.7, 34.4) * mm, "radius": 7 * mm, "construction": true});
            skLineSegment(sketch, "E267.bottom", {"start": v(-17.5, 19.27) * mm, "end": v(17.5, 19.27) * mm, "construction": true});
            skLineSegment(sketch, "E267.top", {"start": v(-17.5, -15.73) * mm, "end": v(17.5, -15.73) * mm, "construction": true});
            skLineSegment(sketch, "E267.left", {"start": v(-17.5, 19.27) * mm, "end": v(-17.5, -15.73) * mm, "construction": true});
            skLineSegment(sketch, "E268", {"start": v(65, 84.27) * mm, "end": v(79, 84.27) * mm, "construction": true});
            skLineSegment(sketch, "E269", {"start": v(65, 84.27) * mm, "end": v(65, 98.27) * mm, "construction": true});
            skCircle(sketch, "E270", {"center": v(65, 93.77) * mm, "radius": 1.5 * mm, "construction": true});
            skCircle(sketch, "E271", {"center": v(65, 92.27) * mm, "radius": 1.5 * mm, "construction": true});
            skCircle(sketch, "E272", {"center": v(57, 84.27) * mm, "radius": 1.5 * mm, "construction": true});
            skCircle(sketch, "E273", {"center": v(55.5, 84.27) * mm, "radius": 1.5 * mm, "construction": true});
            skCircle(sketch, "E274", {"center": v(65, 76.27) * mm, "radius": 1.5 * mm, "construction": true});
            skCircle(sketch, "E275", {"center": v(65, 74.77) * mm, "radius": 1.5 * mm, "construction": true});
            skCircle(sketch, "E276", {"center": v(73, 84.27) * mm, "radius": 1.5 * mm, "construction": true});
            skCircle(sketch, "E277", {"center": v(74.5, 84.27) * mm, "radius": 1.5 * mm, "construction": true});
            skCircle(sketch, "E278", {"center": v(65, 84.27) * mm, "radius": 15.5 * mm, "construction": true});
            skCircle(sketch, "E279", {"center": v(65, 84.27) * mm, "radius": 20 * mm, "construction": true});
            skCircle(sketch, "E280", {"center": v(65, 84.27) * mm, "radius": 23.5 * mm, "construction": true});
            skLineSegment(sketch, "E281", {"start": v(65, 98.27) * mm, "end": v(65, 107.77) * mm, "construction": true});
            skLineSegment(sketch, "E282", {"start": v(79, 84.27) * mm, "end": v(88.5, 84.27) * mm, "construction": true});
            skLineSegment(sketch, "E283", {"start": v(61, 103.86) * mm, "end": v(65, 103.86) * mm, "construction": true});
            skCircle(sketch, "E284", {"center": v(25.7, 34.4) * mm, "radius": 1.5 * mm});
            skLineSegment(sketch, "E285", {"start": v(56.34, 73.27) * mm, "end": v(51.62, 76.98) * mm, "construction": true});
            skLineSegment(sketch, "E286", {"start": v(56.34, 73.27) * mm, "end": v(61.05, 69.56) * mm, "construction": true});
            skLineSegment(sketch, "E287", {"start": v(51.62, 76.98) * mm, "end": v(23.22, 40.94) * mm, "construction": true});
            skLineSegment(sketch, "E288", {"start": v(61.05, 69.56) * mm, "end": v(32.64, 33.5) * mm, "construction": true});
            skLineSegment(sketch, "E289", {"start": v(23.22, 40.94) * mm, "end": v(18.75, 35.26) * mm, "construction": true});
            skLineSegment(sketch, "E290", {"start": v(32.64, 33.5) * mm, "end": v(28.19, 27.85) * mm, "construction": true});
            skLineSegment(sketch, "E291", {"start": v(65, 84.27) * mm, "end": v(57.54, 90.15) * mm, "construction": true});
            skLineSegment(sketch, "E292", {"start": v(65, 84.27) * mm, "end": v(72.46, 78.39) * mm, "construction": true});
            skLineSegment(sketch, "E293", {"start": v(49.82, 74.7) * mm, "end": v(59.25, 67.28) * mm, "construction": true});
            skLineSegment(sketch, "E294", {"start": v(65, 84.27) * mm, "end": v(70.88, 91.73) * mm, "construction": true});
            skLineSegment(sketch, "E295", {"start": v(23.22, 40.94) * mm, "end": v(49.82, 74.7) * mm});
            skLineSegment(sketch, "E296", {"start": v(32.64, 33.5) * mm, "end": v(59.25, 67.28) * mm});
            skArc(sketch, "E297", {"start": v(23.22, 40.94) * mm, "mid": v(20.2, 38.72) * mm, "end": v(18.75, 35.26) * mm});
            skArc(sketch, "E298", {"start": v(28.19, 27.85) * mm, "mid": v(31.2, 30.06) * mm, "end": v(32.64, 33.5) * mm});
            skLineSegment(sketch, "E299", {"start": v(0, 1.77) * mm, "end": v(0, 19.27) * mm, "construction": true});
            skLineSegment(sketch, "E300", {"start": v(0, 1.77) * mm, "end": v(11.81, 1.77) * mm, "construction": true});
            skPoint(sketch, "E301", {"position": v(69.95, 90.55) * mm});
            skLineSegment(sketch, "E302", {"start": v(57.54, 90.15) * mm, "end": v(46.54, 98.81) * mm, "construction": true});
            skLineSegment(sketch, "E303", {"start": v(72.46, 78.39) * mm, "end": v(83.46, 69.73) * mm, "construction": true});
            skLineSegment(sketch, "E304", {"start": v(70.88, 91.73) * mm, "end": v(79.54, 102.73) * mm, "construction": true});
            skFitSpline(sketch, "E305", {"points": [v(59.25, 67.28) * mm, v(65, 68.77) * mm], "startDerivative": vector(3.08, 3.9) * mm, "endDerivative": vector(6.7, 0.89) * mm});
            skCircle(sketch, "E306", {"center": v(65, 84.27) * mm, "radius": 4.5 * mm});
            skArc(sketch, "E307", {"start": v(66.3, 93.02) * mm, "mid": v(65, 95.27) * mm, "end": v(63.7, 93.02) * mm});
            skArc(sketch, "E308", {"start": v(63.7, 93.02) * mm, "mid": v(65, 90.77) * mm, "end": v(66.3, 93.02) * mm});
            skArc(sketch, "E309", {"start": v(73.75, 85.57) * mm, "mid": v(71.5, 84.27) * mm, "end": v(73.75, 82.97) * mm});
            skArc(sketch, "E310", {"start": v(73.75, 82.97) * mm, "mid": v(76, 84.27) * mm, "end": v(73.75, 85.57) * mm});
            skArc(sketch, "E311", {"start": v(66.3, 75.52) * mm, "mid": v(65, 77.77) * mm, "end": v(63.7, 75.52) * mm});
            skArc(sketch, "E312", {"start": v(63.7, 75.52) * mm, "mid": v(65, 73.27) * mm, "end": v(66.3, 75.52) * mm});
            skArc(sketch, "E313", {"start": v(56.25, 82.97) * mm, "mid": v(58.5, 84.27) * mm, "end": v(56.25, 85.57) * mm});
            skArc(sketch, "E314", {"start": v(56.25, 85.57) * mm, "mid": v(54, 84.27) * mm, "end": v(56.25, 82.97) * mm});
            skLineSegment(sketch, "E315", {"start": v(65, 84.27) * mm, "end": v(72.94, 92.2) * mm, "construction": true});
            skPoint(sketch, "E316", {"position": v(70.66, 89.93) * mm});
            skLineSegment(sketch, "E317", {"start": v(65, 103.86) * mm, "end": v(69, 103.86) * mm, "construction": true});
            skFitSpline(sketch, "E318", {"points": [v(61, 103.86) * mm, v(65, 107.77) * mm, v(69, 103.86) * mm], "startDerivative": vector(4.32, 6.84) * mm, "endDerivative": vector(4.23, -8.2) * mm});
            skFitSpline(sketch, "E319", {"points": [v(65, 68.77) * mm, v(85, 84.27) * mm, v(78.04, 89.36) * mm], "startDerivative": vector(42.4, 0.01) * mm, "endDerivative": vector(-28.12, 12.03) * mm});
            skFitSpline(sketch, "E320", {"points": [v(69, 103.86) * mm, v(73.66, 95.27) * mm], "startDerivative": vector(4.66, -8.6) * mm, "endDerivative": vector(4.66, -8.6) * mm});
            skLineSegment(sketch, "E321", {"start": v(65, 98.27) * mm, "end": v(62.3, 98.27) * mm, "construction": true});
            skLineSegment(sketch, "E322", {"start": v(65, 98.27) * mm, "end": v(67.7, 98.27) * mm, "construction": true});
            skFitSpline(sketch, "E323", {"points": [v(62.3, 98.27) * mm, v(65, 101.9) * mm, v(67.7, 98.27) * mm], "startDerivative": vector(5.4, 10.92) * mm, "endDerivative": vector(5.4, -10.92) * mm});
            skFitSpline(sketch, "E324", {"points": [v(62.3, 98.27) * mm, v(65, 98.24) * mm, v(67.7, 98.27) * mm], "startDerivative": vector(-2.5, -4.54) * mm, "endDerivative": vector(-2.5, 4.54) * mm});
            skLineSegment(sketch, "E325", {"start": v(61.88, 97.51) * mm, "end": v(65, 97.51) * mm, "construction": true});
            skLineSegment(sketch, "E326", {"start": v(65, 97.51) * mm, "end": v(68.12, 97.51) * mm, "construction": true});
            skArc(sketch, "E327", {"start": v(78.04, 89.36) * mm, "mid": v(76.25, 92.6) * mm, "end": v(73.66, 95.27) * mm});
            skFitSpline(sketch, "E328", {"points": [v(61, 103.86) * mm, v(56.72, 95.56) * mm], "startDerivative": vector(-4.27, -8.31) * mm, "endDerivative": vector(-4.27, -8.31) * mm});
            skFitSpline(sketch, "E329", {"points": [v(80.74, 85.08) * mm, v(77.9, 78.85) * mm], "startDerivative": vector(3.16, -5.47) * mm, "endDerivative": vector(-4.38, -4.48) * mm});
            skFitSpline(sketch, "E330", {"points": [v(77.9, 78.85) * mm, v(80.74, 85.08) * mm], "startDerivative": vector(-12.2, -14.17) * mm, "endDerivative": vector(6.15, -8.54) * mm});
            skLineSegment(sketch, "E331", {"start": v(13.79, 19.27) * mm, "end": v(0, 19.27) * mm, "construction": true});
            skCircle(sketch, "E332", {"center": v(15.9, 16.32) * mm, "radius": 1.5 * mm});
            skCircle(sketch, "E333", {"center": v(15.9, 16.32) * mm, "radius": 4.5 * mm, "construction": true});
            skLineSegment(sketch, "E334", {"start": v(18.75, 35.26) * mm, "end": v(14.24, 20.5) * mm});
            skLineSegment(sketch, "E335", {"start": v(14.24, 20.5) * mm, "end": v(11.44, 16.96) * mm, "construction": true});
            skLineSegment(sketch, "E336", {"start": v(14.24, 20.5) * mm, "end": v(20.35, 15.68) * mm, "construction": true});
            skLineSegment(sketch, "E337", {"start": v(11.44, 16.96) * mm, "end": v(17.56, 12.14) * mm, "construction": true});
            skLineSegment(sketch, "E338", {"start": v(17.56, 12.14) * mm, "end": v(20.35, 15.68) * mm, "construction": true});
            skLineSegment(sketch, "E339", {"start": v(28.19, 27.85) * mm, "end": v(20.35, 15.68) * mm});
            skLineSegment(sketch, "E340", {"start": v(0, 1.77) * mm, "end": v(0, 6.27) * mm});
            skLineSegment(sketch, "E341", {"start": v(0, 1.77) * mm, "end": v(4.5, 1.77) * mm});
            skLineSegment(sketch, "E342", {"start": v(0, 6.27) * mm, "end": v(11.44, 16.96) * mm});
            skLineSegment(sketch, "E343", {"start": v(4.5, 1.77) * mm, "end": v(17.56, 12.14) * mm});
            skArc(sketch, "E344", {"start": v(17.56, 12.14) * mm, "mid": v(19.43, 13.54) * mm, "end": v(20.35, 15.68) * mm});
            skArc(sketch, "E345", {"start": v(14.24, 20.5) * mm, "mid": v(12.36, 19.1) * mm, "end": v(11.44, 16.96) * mm});
            skLineSegment(sketch, "E346", {"start": v(15.9, 16.32) * mm, "end": v(0, 16.32) * mm, "construction": true});
            skLineSegment(sketch, "E347", {"start": v(15.9, 16.32) * mm, "end": v(15.9, 1.77) * mm, "construction": true});
            skFitSpline(sketch, "E348", {"points": [v(56.72, 95.56) * mm, v(49.5, 84.27) * mm], "startDerivative": vector(-3.81, -8.1) * mm, "endDerivative": vector(-5.07, -18.51) * mm});
            skFitSpline(sketch, "E349", {"points": [v(49.5, 84.27) * mm, v(49.82, 74.7) * mm], "startDerivative": vector(-2.57, -11.14) * mm, "endDerivative": vector(-2.88, -6.17) * mm});
            skSolve(sketch);
        }
        {
            var Q0;
            Q0 = qSketchRegion(id + "F2", true);
            extrude(context, id + "F3", {"entities" : qUnion([Q0]), "oppositeDirection" : true, "depth" : 4 * mm});
        }
        {
            var Q0;
            Q0=qCreatedBy(makeId("Top.planeOp"),FACE);
            var sketch = newSketch(context, id + "F4", { "sketchPlane" : qUnion([Q0])});
            skPoint(sketch, "E350.middle", {"position": v(-2.33, 0.15) * mm});
            skLineSegment(sketch, "E351.bottom", {"start": v(23.37, 32.78) * mm, "end": v(-28.03, 32.78) * mm, "construction": true});
            skLineSegment(sketch, "E351.top", {"start": v(23.37, -32.47) * mm, "end": v(-28.03, -32.47) * mm, "construction": true});
            skLineSegment(sketch, "E351.left", {"start": v(23.37, 32.78) * mm, "end": v(23.37, -32.47) * mm, "construction": true});
            skLineSegment(sketch, "E351.right", {"start": v(-28.03, 32.78) * mm, "end": v(-28.03, -32.47) * mm, "construction": true});
            skLineSegment(sketch, "E352.bottom", {"start": v(-67.33, 82.65) * mm, "end": v(62.67, 82.65) * mm, "construction": true});
            skLineSegment(sketch, "E352.top", {"start": v(-67.33, -82.35) * mm, "end": v(62.67, -82.35) * mm, "construction": true});
            skLineSegment(sketch, "E352.left", {"start": v(-67.33, 82.65) * mm, "end": v(-67.33, -82.35) * mm, "construction": true});
            skLineSegment(sketch, "E352.right", {"start": v(62.67, 82.65) * mm, "end": v(62.67, -82.35) * mm, "construction": true});
            skCircle(sketch, "E353", {"center": v(62.67, 82.65) * mm, "radius": 4.5 * mm, "construction": true});
            skCircle(sketch, "E354", {"center": v(-67.33, 82.65) * mm, "radius": 4.5 * mm, "construction": true});
            skCircle(sketch, "E355", {"center": v(62.67, -82.35) * mm, "radius": 4.5 * mm, "construction": true});
            skCircle(sketch, "E356", {"center": v(-67.33, -82.35) * mm, "radius": 4.5 * mm, "construction": true});
            skCircle(sketch, "E357", {"center": v(62.67, 82.65) * mm, "radius": 8 * mm, "construction": true});
            skCircle(sketch, "E358", {"center": v(62.67, -82.35) * mm, "radius": 8 * mm, "construction": true});
            skCircle(sketch, "E359", {"center": v(-67.33, -82.35) * mm, "radius": 8 * mm, "construction": true});
            skCircle(sketch, "E360", {"center": v(-67.33, 82.65) * mm, "radius": 8 * mm, "construction": true});
            skCircle(sketch, "E361", {"center": v(62.67, 82.65) * mm, "radius": 9.5 * mm, "construction": true});
            skCircle(sketch, "E362", {"center": v(62.67, -82.35) * mm, "radius": 9.5 * mm, "construction": true});
            skCircle(sketch, "E363", {"center": v(-67.33, -82.35) * mm, "radius": 9.5 * mm, "construction": true});
            skCircle(sketch, "E364", {"center": v(-67.33, 82.65) * mm, "radius": 9.5 * mm, "construction": true});
            skCircle(sketch, "E365", {"center": v(62.67, 82.65) * mm, "radius": 14 * mm, "construction": true});
            skCircle(sketch, "E366", {"center": v(-67.33, 82.65) * mm, "radius": 14 * mm, "construction": true});
            skCircle(sketch, "E367", {"center": v(62.67, -82.35) * mm, "radius": 14 * mm, "construction": true});
            skCircle(sketch, "E368", {"center": v(-67.33, -82.35) * mm, "radius": 14 * mm, "construction": true});
            skCircle(sketch, "E369", {"center": v(62.67, 82.65) * mm, "radius": 63.5 * mm, "construction": true});
            skCircle(sketch, "E370", {"center": v(62.67, -82.35) * mm, "radius": 63.5 * mm, "construction": true});
            skCircle(sketch, "E371", {"center": v(-67.33, -82.35) * mm, "radius": 63.5 * mm, "construction": true});
            skCircle(sketch, "E372", {"center": v(-67.33, 82.65) * mm, "radius": 63.5 * mm, "construction": true});
            skLineSegment(sketch, "E373.bottom", {"start": v(-28.52, 26.34) * mm, "end": v(23.86, 26.34) * mm, "construction": true});
            skLineSegment(sketch, "E373.top", {"start": v(-28.52, -26.04) * mm, "end": v(23.86, -26.04) * mm, "construction": true});
            skLineSegment(sketch, "E373.left", {"start": v(-28.52, 26.34) * mm, "end": v(-28.52, -26.04) * mm, "construction": true});
            skLineSegment(sketch, "E373.right", {"start": v(23.86, 26.34) * mm, "end": v(23.86, -26.04) * mm, "construction": true});
            skCircle(sketch, "E374", {"center": v(23.37, 32.78) * mm, "radius": 1.5 * mm, "construction": true});
            skCircle(sketch, "E375", {"center": v(-28.03, 32.78) * mm, "radius": 1.5 * mm, "construction": true});
            skCircle(sketch, "E376", {"center": v(23.37, -32.47) * mm, "radius": 1.5 * mm, "construction": true});
            skCircle(sketch, "E377", {"center": v(-28.03, -32.47) * mm, "radius": 1.5 * mm, "construction": true});
            skLineSegment(sketch, "E378", {"start": v(-67.33, 82.65) * mm, "end": v(62.67, -82.35) * mm, "construction": true});
            skLineSegment(sketch, "E379", {"start": v(62.67, 82.65) * mm, "end": v(-67.33, -82.35) * mm, "construction": true});
            skLineSegment(sketch, "E380.bottom", {"start": v(-17.58, -3.46) * mm, "end": v(12.92, -3.46) * mm, "construction": true});
            skLineSegment(sketch, "E380.top", {"start": v(-17.58, -33.96) * mm, "end": v(12.92, -33.96) * mm, "construction": true});
            skLineSegment(sketch, "E380.left", {"start": v(-17.58, -3.46) * mm, "end": v(-17.58, -33.96) * mm, "construction": true});
            skLineSegment(sketch, "E380.right", {"start": v(12.92, -3.46) * mm, "end": v(12.92, -33.96) * mm, "construction": true});
            skPoint(sketch, "E380.middle", {"position": v(-2.33, -18.71) * mm});
            skLineSegment(sketch, "E381.bottom", {"start": v(-17.58, 33.04) * mm, "end": v(12.92, 33.04) * mm, "construction": true});
            skLineSegment(sketch, "E381.top", {"start": v(-17.58, 2.54) * mm, "end": v(12.92, 2.54) * mm, "construction": true});
            skLineSegment(sketch, "E381.left", {"start": v(-17.58, 33.04) * mm, "end": v(-17.58, 2.54) * mm, "construction": true});
            skLineSegment(sketch, "E381.right", {"start": v(12.92, 33.04) * mm, "end": v(12.92, 2.54) * mm, "construction": true});
            skPoint(sketch, "E381.middle", {"position": v(-2.33, 17.79) * mm});
            skLineSegment(sketch, "E382", {"start": v(-2.33, 2.54) * mm, "end": v(-2.33, -3.46) * mm, "construction": true});
            skLineSegment(sketch, "E383", {"start": v(-28.03, 32.78) * mm, "end": v(-22.53, 37.1) * mm, "construction": true});
            skLineSegment(sketch, "E384", {"start": v(-28.03, 32.78) * mm, "end": v(-33.53, 28.44) * mm, "construction": true});
            skLineSegment(sketch, "E385", {"start": v(-28.03, 32.78) * mm, "end": v(-32.98, 39.06) * mm, "construction": true});
            skLineSegment(sketch, "E386", {"start": v(23.37, 32.78) * mm, "end": v(28.33, 39.06) * mm, "construction": true});
            skLineSegment(sketch, "E387", {"start": v(23.37, 32.78) * mm, "end": v(17.88, 37.1) * mm, "construction": true});
            skLineSegment(sketch, "E388", {"start": v(23.37, 32.78) * mm, "end": v(28.87, 28.44) * mm, "construction": true});
            skLineSegment(sketch, "E389", {"start": v(23.37, -32.47) * mm, "end": v(28.33, -38.75) * mm, "construction": true});
            skLineSegment(sketch, "E390", {"start": v(23.37, -32.47) * mm, "end": v(17.88, -36.8) * mm, "construction": true});
            skLineSegment(sketch, "E391", {"start": v(23.37, -32.47) * mm, "end": v(28.87, -28.13) * mm, "construction": true});
            skLineSegment(sketch, "E392", {"start": v(-28.03, -32.47) * mm, "end": v(-32.98, -38.75) * mm, "construction": true});
            skLineSegment(sketch, "E393", {"start": v(-28.03, -32.47) * mm, "end": v(-22.53, -36.8) * mm, "construction": true});
            skLineSegment(sketch, "E394", {"start": v(-28.03, -32.47) * mm, "end": v(-33.53, -28.13) * mm, "construction": true});
            skFitSpline(sketch, "E395", {"points": [v(-22.53, 37.1) * mm, v(-32.98, 39.06) * mm, v(-33.53, 28.44) * mm], "startDerivative": vector(-20.3, 7.46) * mm, "endDerivative": vector(0.93, -21.61) * mm});
            skFitSpline(sketch, "E396", {"points": [v(17.88, 37.1) * mm, v(28.33, 39.06) * mm, v(28.87, 28.44) * mm], "startDerivative": vector(20.3, 7.46) * mm, "endDerivative": vector(-0.93, -21.61) * mm});
            skPoint(sketch, "E397.visualSharp", {"position": v(-18.08, 35.74) * mm});
            skLineSegment(sketch, "E398", {"start": v(-18.08, 35.74) * mm, "end": v(-2.33, 35.74) * mm, "construction": true});
            skLineSegment(sketch, "E399", {"start": v(-2.33, 35.74) * mm, "end": v(13.42, 35.74) * mm, "construction": true});
            skPoint(sketch, "E400.visualSharp", {"position": v(13.42, 35.74) * mm});
            skLineSegment(sketch, "E401", {"start": v(-2.33, -33.96) * mm, "end": v(-2.33, -37.96) * mm, "construction": true});
            skLineSegment(sketch, "E402", {"start": v(-17.58, -33.96) * mm, "end": v(-21.58, -33.96) * mm, "construction": true});
            skLineSegment(sketch, "E403", {"start": v(12.92, -33.96) * mm, "end": v(16.92, -33.96) * mm, "construction": true});
            skLineSegment(sketch, "E404", {"start": v(-21.58, -38.3) * mm, "end": v(-2.33, -38.3) * mm, "construction": true});
            skLineSegment(sketch, "E405", {"start": v(-2.33, -38.3) * mm, "end": v(16.92, -38.3) * mm, "construction": true});
            skPoint(sketch, "E406.visualSharp", {"position": v(-21.58, -38.3) * mm});
            skPoint(sketch, "E407.visualSharp", {"position": v(16.92, -38.3) * mm});
            skCircle(sketch, "E408", {"center": v(-12.13, -44.75) * mm, "radius": 1.5 * mm});
            skCircle(sketch, "E409", {"center": v(7.47, -44.75) * mm, "radius": 1.5 * mm});
            skLineSegment(sketch, "E410", {"start": v(-12.13, -44.75) * mm, "end": v(-2.33, -44.75) * mm, "construction": true});
            skLineSegment(sketch, "E411", {"start": v(-2.33, -44.75) * mm, "end": v(7.47, -44.75) * mm, "construction": true});
            skFitSpline(sketch, "E412", {"points": [v(-33.53, 28.44) * mm, v(-28.03, 0.15) * mm, v(-33.53, -28.13) * mm], "startDerivative": vector(16.96, -67.18) * mm, "endDerivative": vector(-16.96, -67.18) * mm});
            skFitSpline(sketch, "E413", {"points": [v(28.87, 28.44) * mm, v(23.37, 0.15) * mm, v(28.87, -28.13) * mm], "startDerivative": vector(-16.96, -67.18) * mm, "endDerivative": vector(16.96, -67.18) * mm});
            skLineSegment(sketch, "E414", {"start": v(-2.33, -44.75) * mm, "end": v(-2.33, -50.75) * mm, "construction": true});
            skLineSegment(sketch, "E415", {"start": v(-12.13, -44.75) * mm, "end": v(-16.13, -44.75) * mm, "construction": true});
            skLineSegment(sketch, "E416", {"start": v(-12.13, -44.75) * mm, "end": v(-12.13, -48.75) * mm, "construction": true});
            skLineSegment(sketch, "E417", {"start": v(7.47, -44.75) * mm, "end": v(11.47, -44.75) * mm, "construction": true});
            skLineSegment(sketch, "E418", {"start": v(7.47, -44.75) * mm, "end": v(7.47, -48.75) * mm, "construction": true});
            skCircle(sketch, "E419", {"center": v(-28.03, 32.78) * mm, "radius": 1.5 * mm});
            skCircle(sketch, "E420", {"center": v(23.37, 32.78) * mm, "radius": 1.5 * mm});
            skCircle(sketch, "E421", {"center": v(-28.03, -32.47) * mm, "radius": 1.5 * mm});
            skCircle(sketch, "E422", {"center": v(23.37, -32.47) * mm, "radius": 1.5 * mm});
            skLineSegment(sketch, "E423", {"start": v(115.22, -24.48) * mm, "end": v(115.22, 9.49) * mm, "construction": true});
            skLineSegment(sketch, "E424", {"start": v(-21.37, -36.36) * mm, "end": v(-2.33, -36.36) * mm, "construction": true});
            skLineSegment(sketch, "E425", {"start": v(-2.33, -36.36) * mm, "end": v(16.72, -36.36) * mm, "construction": true});
            skFitSpline(sketch, "E426", {"points": [v(-21.58, -38.3) * mm, v(-16.13, -44.75) * mm, v(-12.13, -48.75) * mm, v(-2.33, -50.75) * mm], "startDerivative": vector(17.01, -18.5) * mm, "endDerivative": vector(29.8, -3.11) * mm});
            skFitSpline(sketch, "E427", {"points": [v(16.92, -38.3) * mm, v(11.47, -44.75) * mm, v(7.47, -48.75) * mm, v(-2.33, -50.75) * mm], "startDerivative": vector(-17.98, -19.6) * mm, "endDerivative": vector(-29.8, -3.11) * mm});
            skLineSegment(sketch, "E428", {"start": v(116.25, 10.49) * mm, "end": v(169.47, 8.84) * mm, "construction": true});
            skPoint(sketch, "E429.visualSharp", {"position": v(115.22, 10.52) * mm});
            skArc(sketch, "E429.filletArc", {"start": v(116.25, 10.49) * mm, "mid": v(115.53, 10.2) * mm, "end": v(115.22, 9.49) * mm, "construction": true});
            skPoint(sketch, "E430.visualSharp", {"position": v(16.72, -36.36) * mm});
            skPoint(sketch, "E431.visualSharp", {"position": v(-21.37, -36.36) * mm});
            skLineSegment(sketch, "E432.bottom", {"start": v(-16.1, 17.65) * mm, "end": v(11.45, 17.65) * mm, "construction": true});
            skLineSegment(sketch, "E432.top", {"start": v(-16.1, -17.35) * mm, "end": v(11.45, -17.35) * mm, "construction": true});
            skLineSegment(sketch, "E432.left", {"start": v(-16.1, 17.65) * mm, "end": v(-16.1, -17.35) * mm, "construction": true});
            skLineSegment(sketch, "E432.right", {"start": v(11.45, 17.65) * mm, "end": v(11.45, -17.35) * mm, "construction": true});
            skLineSegment(sketch, "E433", {"start": v(-2.33, 13.23) * mm, "end": v(-20.53, 13.23) * mm, "construction": true});
            skLineSegment(sketch, "E434", {"start": v(-2.33, 13.23) * mm, "end": v(15.88, 13.23) * mm, "construction": true});
            skLineSegment(sketch, "E435", {"start": v(-2.33, 0.15) * mm, "end": v(-2.33, 14.42) * mm, "construction": true});
            skLineSegment(sketch, "E436", {"start": v(-2.33, 0.15) * mm, "end": v(14.67, 0.15) * mm, "construction": true});
            skLineSegment(sketch, "E437.bottom", {"start": v(-18.22, 14.7) * mm, "end": v(13.57, 14.7) * mm, "construction": true});
            skLineSegment(sketch, "E437.top", {"start": v(-18.22, -14.4) * mm, "end": v(13.57, -14.4) * mm, "construction": true});
            skLineSegment(sketch, "E437.left", {"start": v(-18.22, 14.7) * mm, "end": v(-18.22, -14.4) * mm, "construction": true});
            skLineSegment(sketch, "E437.right", {"start": v(13.57, 14.7) * mm, "end": v(13.57, -14.4) * mm, "construction": true});
            skLineSegment(sketch, "E438", {"start": v(-2.33, 26.07) * mm, "end": v(12, 26.07) * mm, "construction": true});
            skLineSegment(sketch, "E439", {"start": v(-2.33, 26.07) * mm, "end": v(-16.66, 26.07) * mm, "construction": true});
            skPoint(sketch, "E440.middle", {"position": v(-16.66, 26.07) * mm});
            skPoint(sketch, "E441.middle", {"position": v(12, 26.07) * mm});
            skFitSpline(sketch, "E442", {"points": [v(-33.53, -28.13) * mm, v(-32.98, -38.75) * mm, v(-22.93, -36.94) * mm], "startDerivative": vector(-1.92, -24.87) * mm, "endDerivative": vector(23.17, 7.34) * mm});
            skLineSegment(sketch, "E443", {"start": v(-22.93, -36.94) * mm, "end": v(-2.33, -36.94) * mm, "construction": true});
            skLineSegment(sketch, "E444", {"start": v(-2.33, -36.94) * mm, "end": v(18.28, -36.94) * mm, "construction": true});
            skLineSegment(sketch, "E445", {"start": v(16.92, -38.3) * mm, "end": v(17.66, -37.14) * mm});
            skLineSegment(sketch, "E446", {"start": v(18.25, -36.93) * mm, "end": v(18.28, -36.94) * mm});
            skLineSegment(sketch, "E447", {"start": v(-21.58, -38.3) * mm, "end": v(-22.32, -37.14) * mm});
            skLineSegment(sketch, "E448", {"start": v(-22.9, -36.93) * mm, "end": v(-22.93, -36.94) * mm});
            skLineSegment(sketch, "E449", {"start": v(169.47, 8.84) * mm, "end": v(169.47, -13.62) * mm, "construction": true});
            skPoint(sketch, "E450.visualSharp", {"position": v(17.88, -36.8) * mm});
            skArc(sketch, "E450.filletArc", {"start": v(18.25, -36.93) * mm, "mid": v(17.92, -36.93) * mm, "end": v(17.66, -37.14) * mm});
            skPoint(sketch, "E451.visualSharp", {"position": v(-22.53, -36.8) * mm});
            skArc(sketch, "E451.filletArc", {"start": v(-22.32, -37.14) * mm, "mid": v(-22.58, -36.93) * mm, "end": v(-22.9, -36.93) * mm});
            skLineSegment(sketch, "E452", {"start": v(-2.33, 0.15) * mm, "end": v(-2.33, 3.45) * mm, "construction": true});
            skLineSegment(sketch, "E453.bottom", {"start": v(-7.83, 5.65) * mm, "end": v(3.17, 5.65) * mm, "construction": true});
            skLineSegment(sketch, "E453.top", {"start": v(-7.83, -5.35) * mm, "end": v(3.17, -5.35) * mm, "construction": true});
            skLineSegment(sketch, "E453.left", {"start": v(-7.83, 5.65) * mm, "end": v(-7.83, -5.35) * mm, "construction": true});
            skLineSegment(sketch, "E453.right", {"start": v(3.17, 5.65) * mm, "end": v(3.17, -5.35) * mm, "construction": true});
            skLineSegment(sketch, "E454.bottom", {"start": v(-10.3, 10.77) * mm, "end": v(5.65, 10.77) * mm});
            skPoint(sketch, "E454.middle", {"position": v(-2.33, 12.75) * mm});
            skPoint(sketch, "E455.middle", {"position": v(-2.33, -26.45) * mm});
            skPoint(sketch, "E456", {"position": v(-2.33, -17.35) * mm});
            skPoint(sketch, "E457", {"position": v(-2.33, -26.04) * mm});
            skLineSegment(sketch, "E458", {"start": v(-11.02, 12.48) * mm, "end": v(-3.74, 19.76) * mm});
            skLineSegment(sketch, "E459", {"start": v(-0.91, 19.76) * mm, "end": v(6.36, 12.48) * mm});
            skPoint(sketch, "E460.visualSharp", {"position": v(-2.33, 21.17) * mm});
            skArc(sketch, "E460.filletArc", {"start": v(-0.91, 19.76) * mm, "mid": v(-2.33, 20.34) * mm, "end": v(-3.74, 19.76) * mm});
            skPoint(sketch, "E461.visualSharp", {"position": v(-12.72, 10.77) * mm});
            skArc(sketch, "E461.filletArc", {"start": v(-11.02, 12.48) * mm, "mid": v(-11.23, 11.4) * mm, "end": v(-10.3, 10.77) * mm});
            skPoint(sketch, "E462.visualSharp", {"position": v(8.07, 10.77) * mm});
            skArc(sketch, "E462.filletArc", {"start": v(5.65, 10.77) * mm, "mid": v(6.58, 11.4) * mm, "end": v(6.36, 12.48) * mm});
            skPoint(sketch, "E463.visualSharp", {"position": v(-2.33, 0.75) * mm});
            skLineSegment(sketch, "E464", {"start": v(-1.33, 10.77) * mm, "end": v(-1.33, 6.27) * mm, "construction": true});
            skPoint(sketch, "E465.middle", {"position": v(-2.33, 9.75) * mm});
            skCircle(sketch, "E466", {"center": v(13.57, 14.7) * mm, "radius": 4.5 * mm, "construction": true});
            skCircle(sketch, "E467", {"center": v(-18.22, 14.7) * mm, "radius": 4.5 * mm, "construction": true});
            skCircle(sketch, "E468", {"center": v(13.57, -14.4) * mm, "radius": 4.5 * mm, "construction": true});
            skCircle(sketch, "E469", {"center": v(-18.22, -14.4) * mm, "radius": 4.5 * mm, "construction": true});
            skLineSegment(sketch, "E470", {"start": v(-2.33, 0.15) * mm, "end": v(-18.22, 14.7) * mm, "construction": true});
            skLineSegment(sketch, "E471", {"start": v(-2.33, 0.15) * mm, "end": v(13.57, 14.7) * mm, "construction": true});
            skLineSegment(sketch, "E472", {"start": v(13.57, 14.7) * mm, "end": v(23.37, 32.78) * mm, "construction": true});
            skLineSegment(sketch, "E473", {"start": v(-18.22, 14.7) * mm, "end": v(-28.03, 32.78) * mm, "construction": true});
            skLineSegment(sketch, "E474", {"start": v(-2.33, 0.15) * mm, "end": v(-18.22, -14.4) * mm, "construction": true});
            skLineSegment(sketch, "E475", {"start": v(-18.22, -14.4) * mm, "end": v(-28.03, -32.47) * mm, "construction": true});
            skLineSegment(sketch, "E476", {"start": v(-2.33, 0.15) * mm, "end": v(13.57, -14.4) * mm, "construction": true});
            skLineSegment(sketch, "E477", {"start": v(13.57, -14.4) * mm, "end": v(23.37, -32.47) * mm, "construction": true});
            skLineSegment(sketch, "E478", {"start": v(-12.93, 28.63) * mm, "end": v(-12.93, 20.27) * mm});
            skLineSegment(sketch, "E479", {"start": v(8.28, 28.63) * mm, "end": v(8.28, 20.27) * mm});
            skLineSegment(sketch, "E480", {"start": v(-11.23, 19.56) * mm, "end": v(-5.16, 25.63) * mm});
            skLineSegment(sketch, "E481", {"start": v(0.5, 25.63) * mm, "end": v(6.57, 19.56) * mm});
            skPoint(sketch, "E482.visualSharp", {"position": v(-4.57, 37.81) * mm});
            skPoint(sketch, "E483.visualSharp", {"position": v(-12.93, 29.46) * mm});
            skArc(sketch, "E483.filletArc", {"start": v(-12.35, 30.04) * mm, "mid": v(-12.78, 29.4) * mm, "end": v(-12.93, 28.63) * mm});
            skPoint(sketch, "E484.visualSharp", {"position": v(-4.57, 26.22) * mm});
            skArc(sketch, "E484.filletArc", {"start": v(-5.16, 25.63) * mm, "mid": v(-4.73, 26.28) * mm, "end": v(-4.57, 27.04) * mm});
            skPoint(sketch, "E485.visualSharp", {"position": v(-0.08, 26.22) * mm});
            skArc(sketch, "E485.filletArc", {"start": v(-0.08, 27.04) * mm, "mid": v(0.07, 26.28) * mm, "end": v(0.5, 25.63) * mm});
            skPoint(sketch, "E486.visualSharp", {"position": v(8.28, 29.46) * mm});
            skArc(sketch, "E486.filletArc", {"start": v(8.28, 28.63) * mm, "mid": v(8.13, 29.4) * mm, "end": v(7.7, 30.04) * mm});
            skPoint(sketch, "E487.visualSharp", {"position": v(-0.08, 37.81) * mm});
            skPoint(sketch, "E488.visualSharp", {"position": v(8.28, 17.86) * mm});
            skArc(sketch, "E488.filletArc", {"start": v(6.57, 19.56) * mm, "mid": v(7.66, 19.35) * mm, "end": v(8.28, 20.27) * mm});
            skPoint(sketch, "E489.visualSharp", {"position": v(-12.93, 17.86) * mm});
            skArc(sketch, "E489.filletArc", {"start": v(-12.93, 20.27) * mm, "mid": v(-12.32, 19.35) * mm, "end": v(-11.23, 19.56) * mm});
            skLineSegment(sketch, "E490", {"start": v(-2.33, -22.87) * mm, "end": v(-10.31, -22.87) * mm});
            skLineSegment(sketch, "E491", {"start": v(-2.33, -22.87) * mm, "end": v(5.66, -22.87) * mm});
            skLineSegment(sketch, "E492", {"start": v(-11.02, -24.57) * mm, "end": v(-3.74, -31.85) * mm});
            skLineSegment(sketch, "E493", {"start": v(6.37, -24.57) * mm, "end": v(-0.91, -31.85) * mm});
            skPoint(sketch, "E494.visualSharp", {"position": v(8.07, -22.87) * mm});
            skArc(sketch, "E494.filletArc", {"start": v(6.37, -24.57) * mm, "mid": v(6.58, -23.48) * mm, "end": v(5.66, -22.87) * mm});
            skPoint(sketch, "E495.visualSharp", {"position": v(-12.73, -22.87) * mm});
            skArc(sketch, "E495.filletArc", {"start": v(-10.31, -22.87) * mm, "mid": v(-11.24, -23.48) * mm, "end": v(-11.02, -24.57) * mm});
            skPoint(sketch, "E496.visualSharp", {"position": v(-2.33, -33.27) * mm});
            skArc(sketch, "E496.filletArc", {"start": v(-3.74, -31.85) * mm, "mid": v(-2.33, -32.44) * mm, "end": v(-0.91, -31.85) * mm});
            skFitSpline(sketch, "E497", {"points": [v(28.87, -28.13) * mm, v(28.33, -38.75) * mm, v(18.28, -36.94) * mm], "startDerivative": vector(1.93, -24.89) * mm, "endDerivative": vector(-23.2, 7.39) * mm});
            skLineSegment(sketch, "E498", {"start": v(-11.02, -30.5) * mm, "end": v(-6.24, -35.29) * mm});
            skLineSegment(sketch, "E499", {"start": v(6.37, -30.5) * mm, "end": v(1.59, -35.29) * mm});
            skLineSegment(sketch, "E500", {"start": v(-5.66, -36.7) * mm, "end": v(-5.66, -42.34) * mm});
            skLineSegment(sketch, "E501", {"start": v(-7.36, -43.05) * mm, "end": v(-12.14, -38.27) * mm});
            skLineSegment(sketch, "E502", {"start": v(-12.73, -36.85) * mm, "end": v(-12.73, -31.22) * mm});
            skLineSegment(sketch, "E503", {"start": v(1, -36.7) * mm, "end": v(1, -42.34) * mm});
            skLineSegment(sketch, "E504", {"start": v(2.7, -43.05) * mm, "end": v(7.49, -38.27) * mm});
            skLineSegment(sketch, "E505", {"start": v(8.07, -36.85) * mm, "end": v(8.07, -31.22) * mm});
            skPoint(sketch, "E506.visualSharp", {"position": v(8.07, -28.8) * mm});
            skArc(sketch, "E506.filletArc", {"start": v(8.07, -31.22) * mm, "mid": v(7.46, -30.3) * mm, "end": v(6.37, -30.5) * mm});
            skPoint(sketch, "E507.visualSharp", {"position": v(1, -44.75) * mm});
            skArc(sketch, "E507.filletArc", {"start": v(1, -42.34) * mm, "mid": v(1.62, -43.26) * mm, "end": v(2.7, -43.05) * mm});
            skPoint(sketch, "E508.visualSharp", {"position": v(-5.66, -44.75) * mm});
            skArc(sketch, "E508.filletArc", {"start": v(-7.36, -43.05) * mm, "mid": v(-6.27, -43.26) * mm, "end": v(-5.66, -42.34) * mm});
            skPoint(sketch, "E509.visualSharp", {"position": v(-12.73, -28.8) * mm});
            skArc(sketch, "E509.filletArc", {"start": v(-11.02, -30.5) * mm, "mid": v(-12.1, -30.3) * mm, "end": v(-12.73, -31.22) * mm});
            skPoint(sketch, "E510.visualSharp", {"position": v(-5.66, -35.87) * mm});
            skArc(sketch, "E510.filletArc", {"start": v(-5.66, -36.7) * mm, "mid": v(-5.8, -35.94) * mm, "end": v(-6.24, -35.29) * mm});
            skPoint(sketch, "E511.visualSharp", {"position": v(-12.73, -37.68) * mm});
            skArc(sketch, "E511.filletArc", {"start": v(-12.73, -36.85) * mm, "mid": v(-12.57, -37.62) * mm, "end": v(-12.14, -38.27) * mm});
            skPoint(sketch, "E512.visualSharp", {"position": v(1, -35.87) * mm});
            skArc(sketch, "E512.filletArc", {"start": v(1.59, -35.29) * mm, "mid": v(1.15, -35.94) * mm, "end": v(1, -36.7) * mm});
            skPoint(sketch, "E513.visualSharp", {"position": v(8.07, -37.68) * mm});
            skArc(sketch, "E513.filletArc", {"start": v(7.49, -38.27) * mm, "mid": v(7.92, -37.62) * mm, "end": v(8.07, -36.85) * mm});
            skLineSegment(sketch, "E514", {"start": v(-2.33, -18.71) * mm, "end": v(-10.31, -18.71) * mm});
            skLineSegment(sketch, "E515", {"start": v(-2.33, -18.71) * mm, "end": v(5.66, -18.71) * mm});
            skLineSegment(sketch, "E516", {"start": v(-11.02, -17) * mm, "end": v(-3.74, -9.72) * mm});
            skLineSegment(sketch, "E517", {"start": v(6.37, -17) * mm, "end": v(-0.91, -9.72) * mm});
            skPoint(sketch, "E518.visualSharp", {"position": v(-2.33, -8.31) * mm});
            skArc(sketch, "E518.filletArc", {"start": v(-0.91, -9.72) * mm, "mid": v(-2.33, -9.14) * mm, "end": v(-3.74, -9.72) * mm});
            skPoint(sketch, "E519.visualSharp", {"position": v(-12.73, -18.71) * mm});
            skArc(sketch, "E519.filletArc", {"start": v(-11.02, -17) * mm, "mid": v(-11.24, -18.1) * mm, "end": v(-10.31, -18.71) * mm});
            skPoint(sketch, "E520.visualSharp", {"position": v(8.07, -18.71) * mm});
            skArc(sketch, "E520.filletArc", {"start": v(5.66, -18.71) * mm, "mid": v(6.58, -18.1) * mm, "end": v(6.37, -17) * mm});
            skLineSegment(sketch, "E521", {"start": v(14.67, 0.15) * mm, "end": v(17.67, 0.15) * mm, "construction": true});
            skCircle(sketch, "E522", {"center": v(23.37, 32.78) * mm, "radius": 7 * mm, "construction": true});
            skLineSegment(sketch, "E523", {"start": v(17.64, 12.88) * mm, "end": v(21.69, 20.22) * mm});
            skLineSegment(sketch, "E524", {"start": v(22.15, 20.04) * mm, "end": v(18.73, 7.4) * mm});
            skLineSegment(sketch, "E525", {"start": v(16.8, 5.92) * mm, "end": v(12.23, 5.92) * mm});
            skLineSegment(sketch, "E526", {"start": v(11.62, 7.72) * mm, "end": v(16.31, 11.33) * mm});
            skPoint(sketch, "E527.visualSharp", {"position": v(22.7, 22.04) * mm});
            skArc(sketch, "E527.filletArc", {"start": v(22.15, 20.04) * mm, "mid": v(22, 20.33) * mm, "end": v(21.69, 20.22) * mm});
            skPoint(sketch, "E528.visualSharp", {"position": v(18.33, 5.92) * mm});
            skArc(sketch, "E528.filletArc", {"start": v(16.8, 5.92) * mm, "mid": v(18.02, 6.34) * mm, "end": v(18.73, 7.4) * mm});
            skPoint(sketch, "E529.visualSharp", {"position": v(9.29, 5.92) * mm});
            skArc(sketch, "E529.filletArc", {"start": v(11.62, 7.72) * mm, "mid": v(11.28, 6.6) * mm, "end": v(12.23, 5.92) * mm});
            skPoint(sketch, "E530.visualSharp", {"position": v(17.14, 11.97) * mm});
            skArc(sketch, "E530.filletArc", {"start": v(16.31, 11.33) * mm, "mid": v(17.06, 12.04) * mm, "end": v(17.64, 12.88) * mm});
            skLineSegment(sketch, "E531", {"start": v(9.29, 5.92) * mm, "end": v(-2.33, 5.92) * mm, "construction": true});
            skPoint(sketch, "E531.endSnap0", {"position": v(-2.33, 5.65) * mm});
            skLineSegment(sketch, "E532", {"start": v(-2.33, 5.92) * mm, "end": v(-13.94, 5.92) * mm, "construction": true});
            skLineSegment(sketch, "E533", {"start": v(-16.88, 5.92) * mm, "end": v(-21.46, 5.92) * mm});
            skLineSegment(sketch, "E534", {"start": v(17.14, 11.97) * mm, "end": v(-2.33, 11.97) * mm, "construction": true});
            skLineSegment(sketch, "E535", {"start": v(-2.33, 11.97) * mm, "end": v(-21.8, 11.97) * mm, "construction": true});
            skLineSegment(sketch, "E536", {"start": v(22.7, 22.04) * mm, "end": v(-2.33, 22.04) * mm, "construction": true});
            skLineSegment(sketch, "E537", {"start": v(-2.33, 22.04) * mm, "end": v(-27.34, 22.04) * mm, "construction": true});
            skLineSegment(sketch, "E538", {"start": v(-26.8, 20.04) * mm, "end": v(-23.39, 7.4) * mm});
            skLineSegment(sketch, "E539", {"start": v(-16.27, 7.72) * mm, "end": v(-20.97, 11.33) * mm});
            skLineSegment(sketch, "E540", {"start": v(-22.3, 12.88) * mm, "end": v(-26.34, 20.22) * mm});
            skPoint(sketch, "E541.visualSharp", {"position": v(-27.34, 22.04) * mm});
            skArc(sketch, "E541.filletArc", {"start": v(-26.34, 20.22) * mm, "mid": v(-26.65, 20.33) * mm, "end": v(-26.8, 20.04) * mm});
            skPoint(sketch, "E542.visualSharp", {"position": v(-13.94, 5.92) * mm});
            skArc(sketch, "E542.filletArc", {"start": v(-16.88, 5.92) * mm, "mid": v(-15.93, 6.6) * mm, "end": v(-16.27, 7.72) * mm});
            skPoint(sketch, "E543.visualSharp", {"position": v(-22.99, 5.92) * mm});
            skArc(sketch, "E543.filletArc", {"start": v(-23.39, 7.4) * mm, "mid": v(-22.67, 6.34) * mm, "end": v(-21.46, 5.92) * mm});
            skPoint(sketch, "E544.visualSharp", {"position": v(-21.8, 11.97) * mm});
            skArc(sketch, "E544.filletArc", {"start": v(-22.3, 12.88) * mm, "mid": v(-21.71, 12.04) * mm, "end": v(-20.97, 11.33) * mm});
            skFitSpline(sketch, "E545", {"points": [v(-22.53, 37.1) * mm, v(-2.33, 38.28) * mm, v(17.88, 37.1) * mm], "startDerivative": vector(40.4, 3.51) * mm, "endDerivative": vector(40.4, -3.51) * mm});
            skLineSegment(sketch, "E546", {"start": v(-0.08, 27.04) * mm, "end": v(-0.08, 30.57) * mm});
            skLineSegment(sketch, "E547", {"start": v(5.04, 32.7) * mm, "end": v(7.7, 30.04) * mm});
            skArc(sketch, "E548.filletArc", {"start": v(5.04, 32.7) * mm, "mid": v(1.77, 33.34) * mm, "end": v(-0.08, 30.57) * mm});
            skLineSegment(sketch, "E549", {"start": v(-12.35, 30.04) * mm, "end": v(-9.7, 32.7) * mm});
            skLineSegment(sketch, "E550", {"start": v(-4.57, 27.04) * mm, "end": v(-4.57, 30.57) * mm});
            skArc(sketch, "E551.filletArc", {"start": v(-4.57, 30.57) * mm, "mid": v(-6.43, 33.34) * mm, "end": v(-9.7, 32.7) * mm});
            skLineSegment(sketch, "E552", {"start": v(-2.33, 0.15) * mm, "end": v(-32.46, 0.15) * mm, "construction": true});
            skLineSegment(sketch, "E553", {"start": v(-27.34, 22.04) * mm, "end": v(-27.34, 0.15) * mm, "construction": true});
            skLineSegment(sketch, "E554", {"start": v(-27.34, 0.15) * mm, "end": v(-27.34, -21.73) * mm, "construction": true});
            skLineSegment(sketch, "E555", {"start": v(-21.8, 11.97) * mm, "end": v(-21.8, 0.15) * mm, "construction": true});
            skLineSegment(sketch, "E556", {"start": v(-21.8, 0.15) * mm, "end": v(-21.8, -11.66) * mm, "construction": true});
            skLineSegment(sketch, "E557", {"start": v(-22.99, 5.92) * mm, "end": v(-22.99, 0.15) * mm, "construction": true});
            skLineSegment(sketch, "E558", {"start": v(-22.99, 0.15) * mm, "end": v(-22.99, -5.62) * mm, "construction": true});
            skLineSegment(sketch, "E559", {"start": v(-13.94, 5.92) * mm, "end": v(-13.94, 0.15) * mm, "construction": true});
            skLineSegment(sketch, "E560", {"start": v(-13.94, 0.15) * mm, "end": v(-13.94, -5.62) * mm, "construction": true});
            skLineSegment(sketch, "E561", {"start": v(-26.8, -19.73) * mm, "end": v(-23.39, -7.1) * mm});
            skLineSegment(sketch, "E562", {"start": v(-21.46, -5.62) * mm, "end": v(-16.88, -5.62) * mm});
            skLineSegment(sketch, "E563", {"start": v(-16.27, -7.4) * mm, "end": v(-20.97, -11.02) * mm});
            skLineSegment(sketch, "E564", {"start": v(-22.3, -12.57) * mm, "end": v(-26.34, -19.91) * mm});
            skPoint(sketch, "E565.visualSharp", {"position": v(-22.99, -5.62) * mm});
            skArc(sketch, "E565.filletArc", {"start": v(-21.46, -5.62) * mm, "mid": v(-22.67, -6.03) * mm, "end": v(-23.39, -7.1) * mm});
            skPoint(sketch, "E566.visualSharp", {"position": v(-27.34, -21.73) * mm});
            skArc(sketch, "E566.filletArc", {"start": v(-26.8, -19.73) * mm, "mid": v(-26.65, -20.02) * mm, "end": v(-26.34, -19.91) * mm});
            skPoint(sketch, "E567.visualSharp", {"position": v(-13.94, -5.62) * mm});
            skArc(sketch, "E567.filletArc", {"start": v(-16.27, -7.4) * mm, "mid": v(-15.93, -6.3) * mm, "end": v(-16.88, -5.62) * mm});
            skPoint(sketch, "E568.visualSharp", {"position": v(-21.8, -11.66) * mm});
            skArc(sketch, "E568.filletArc", {"start": v(-20.97, -11.02) * mm, "mid": v(-21.71, -11.73) * mm, "end": v(-22.3, -12.57) * mm});
            skLineSegment(sketch, "E569", {"start": v(17.67, 0.15) * mm, "end": v(33.38, 0.15) * mm, "construction": true});
            skLineSegment(sketch, "E570", {"start": v(22.7, 22.04) * mm, "end": v(22.7, 0.15) * mm, "construction": true});
            skLineSegment(sketch, "E571", {"start": v(22.7, 0.15) * mm, "end": v(22.7, -21.73) * mm, "construction": true});
            skLineSegment(sketch, "E572", {"start": v(17.14, 11.97) * mm, "end": v(17.14, 0.15) * mm, "construction": true});
            skLineSegment(sketch, "E573", {"start": v(17.14, 0.15) * mm, "end": v(17.14, -11.66) * mm, "construction": true});
            skLineSegment(sketch, "E574", {"start": v(18.33, 5.92) * mm, "end": v(18.33, 0.15) * mm, "construction": true});
            skLineSegment(sketch, "E575", {"start": v(18.33, 0.15) * mm, "end": v(18.33, -5.62) * mm, "construction": true});
            skLineSegment(sketch, "E576", {"start": v(9.29, 5.92) * mm, "end": v(9.29, 0.15) * mm, "construction": true});
            skLineSegment(sketch, "E577", {"start": v(9.29, 0.15) * mm, "end": v(9.29, -5.62) * mm, "construction": true});
            skLineSegment(sketch, "E578", {"start": v(22.15, -19.73) * mm, "end": v(18.73, -7.1) * mm});
            skLineSegment(sketch, "E579", {"start": v(16.8, -5.62) * mm, "end": v(12.23, -5.62) * mm});
            skLineSegment(sketch, "E580", {"start": v(11.62, -7.4) * mm, "end": v(16.31, -11.02) * mm});
            skLineSegment(sketch, "E581", {"start": v(17.64, -12.57) * mm, "end": v(21.69, -19.91) * mm});
            skPoint(sketch, "E582.visualSharp", {"position": v(22.7, -21.73) * mm});
            skArc(sketch, "E582.filletArc", {"start": v(21.69, -19.91) * mm, "mid": v(22, -20.02) * mm, "end": v(22.15, -19.73) * mm});
            skPoint(sketch, "E583.visualSharp", {"position": v(9.29, -5.62) * mm});
            skArc(sketch, "E583.filletArc", {"start": v(12.23, -5.62) * mm, "mid": v(11.28, -6.3) * mm, "end": v(11.62, -7.4) * mm});
            skPoint(sketch, "E584.visualSharp", {"position": v(18.33, -5.62) * mm});
            skArc(sketch, "E584.filletArc", {"start": v(18.73, -7.1) * mm, "mid": v(18.02, -6.03) * mm, "end": v(16.8, -5.62) * mm});
            skPoint(sketch, "E585.visualSharp", {"position": v(17.14, -11.66) * mm});
            skArc(sketch, "E585.filletArc", {"start": v(17.64, -12.57) * mm, "mid": v(17.06, -11.73) * mm, "end": v(16.31, -11.02) * mm});
            skSolve(sketch);
        }
        {
            var Q0;
            Q0 = qSketchRegion(id + "F4", true);
            extrude(context, id + "F5", {"entities" : qUnion([Q0]), "oppositeDirection" : true, "depth" : 10 * mm, "hasSecondDirection" : true, "secondDirectionOppositeDirection" : true, "secondDirectionDepth" : 8 * mm});
        }
    });
